FCSTD DOCUMENT  (FreeCAD 0.21R33694 (Git))
Label: charger
License: All rights reserved
LicenseURL: http://en.wikipedia.org/wiki/All_rights_reserved
objects: Part::Feature×111, App::Part×21, Sketcher::SketchObject×17, PartDesign::Pocket×9, PartDesign::Pad×8, PartDesign::Fillet×7, Part::FeaturePython×5, Part::Box×2, PartDesign::Body×2, App::DocumentObjectGroup×1
note: 185 computed .brp shape members not serialized (recipe doc carries the construction recipe); baked Part::Feature solids carry a one-line shape summary decoded from their .brp

FEATURE [Part::Box] Box002  label="Cube002"
  AttacherType = Attacher::AttachEngine3D
  Height = 13
  Length = 9
  Placement = pos=(3.5,14,-13) rot=(0,0,1;0rad)
  Width = 9
FEATURE [Part::Box] Box003  label="Cube003"
  AttacherType = Attacher::AttachEngine3D
  Height = 6
  Length = 10
  Placement = pos=(2.5,3,-6) rot=(0,0,1;0rad)
  Width = 6
FEATURE [Part::Feature] Part__Feature  label="v & a metr"
  shape: bbox 48 x 28.9 x 21.79 mm, 178 faces (baked)
FEATURE [App::Part] Part  label="VA indicator"
  Group = -> [Box002,Box003,Part__Feature]
  Origin = -> Origin
FEATURE [Part::Feature] Part__Feature001  label="Basetta"
  shape: bbox 51 x 26 x 1.7 mm, 150 faces (baked)
FEATURE [Part::Feature] Part__Feature002  label="DG301-5.0-02 v1"
  Placement = pos=(4,19.4,1.6) rot=(0,0,-1;1.5708rad)
  shape: bbox 7.6 x 10.6 x 10 mm, 75 faces (baked)
FEATURE [Part::Feature] Part__Feature003  label="DG301-5.0-02 v002"
  Placement = pos=(4,19.4,1.6) rot=(0,0,-1;1.5708rad)
  shape: bbox 4.003 x 4.003 x 9.803 mm, 11 faces (baked)
FEATURE [Part::Feature] Part__Feature004  label="DG301-5.0-02 v003"
  Placement = pos=(4,19.4,1.6) rot=(0,0,-1;1.5708rad)
  shape: bbox 5.55 x 3.9 x 2.851 mm, 29 faces (baked)
FEATURE [Part::Feature] Part__Feature005  label="DG301-5.0-02 v004"
  Placement = pos=(4,19.4,1.6) rot=(0,0,-1;1.5708rad)
  shape: bbox 3.898 x 3.8 x 5.801 mm, 14 faces (baked)
FEATURE [Part::Feature] Part__Feature006  label="DG301-5.0-02 v005"
  Placement = pos=(4,19.4,1.6) rot=(0,0,-1;1.5708rad)
  shape: bbox 4.003 x 4.003 x 9.803 mm, 11 faces (baked)
FEATURE [Part::Feature] Part__Feature007  label="DG301-5.0-02 v006"
  Placement = pos=(4,19.4,1.6) rot=(0,0,-1;1.5708rad)
  shape: bbox 5.55 x 3.9 x 2.851 mm, 29 faces (baked)
FEATURE [Part::Feature] Part__Feature008  label="DG301-5.0-02 v007"
  Placement = pos=(4,19.4,1.6) rot=(0,0,-1;1.5708rad)
  shape: bbox 3.898 x 3.8 x 5.801 mm, 14 faces (baked)
FEATURE [App::Part] DG301_5_0_02_v1  label="DG301-5.0-02 v008"
  Group = -> [Part__Feature002,Part__Feature003,Part__Feature004,Part__Feature005,Part__Feature006,Part__Feature007,Part__Feature008]
  Origin = -> Origin001
FEATURE [Part::Feature] Part__Feature009  label="DG301-5.0-02 v009"
  Placement = pos=(47,6.6,1.6) rot=(0,0,1;1.5708rad)
  shape: bbox 7.6 x 10.6 x 10 mm, 75 faces (baked)
FEATURE [Part::Feature] Part__Feature010  label="DG301-5.0-02 v010"
  Placement = pos=(47,6.6,1.6) rot=(0,0,1;1.5708rad)
  shape: bbox 4.003 x 4.003 x 9.803 mm, 11 faces (baked)
FEATURE [Part::Feature] Part__Feature011  label="DG301-5.0-02 v011"
  Placement = pos=(47,6.6,1.6) rot=(0,0,1;1.5708rad)
  shape: bbox 5.55 x 3.9 x 2.851 mm, 29 faces (baked)
FEATURE [Part::Feature] Part__Feature012  label="DG301-5.0-02 v012"
  Placement = pos=(47,6.6,1.6) rot=(0,0,1;1.5708rad)
  shape: bbox 3.898 x 3.8 x 5.801 mm, 14 faces (baked)
FEATURE [Part::Feature] Part__Feature013  label="DG301-5.0-02 v013"
  Placement = pos=(47,6.6,1.6) rot=(0,0,1;1.5708rad)
  shape: bbox 4.003 x 4.003 x 9.803 mm, 11 faces (baked)
FEATURE [Part::Feature] Part__Feature014  label="DG301-5.0-02 v014"
  Placement = pos=(47,6.6,1.6) rot=(0,0,1;1.5708rad)
  shape: bbox 5.55 x 3.9 x 2.851 mm, 29 faces (baked)
FEATURE [Part::Feature] Part__Feature015  label="DG301-5.0-02 v015"
  Placement = pos=(47,6.6,1.6) rot=(0,0,1;1.5708rad)
  shape: bbox 3.898 x 3.8 x 5.801 mm, 14 faces (baked)
FEATURE [App::Part] DG301_5_0_02_v002  label="DG301-5.0-02 v016"
  Group = -> [Part__Feature009,Part__Feature010,Part__Feature011,Part__Feature012,Part__Feature013,Part__Feature014,Part__Feature015]
  Origin = -> Origin002
FEATURE [Part::Feature] Part__Feature016  label="CAPACITOR 10x10 SMD v1"
  Placement = pos=(9.325,5.925,1.6) rot=(1,0,0;1.5708rad)
  shape: bbox 1 x 2 x 0.2 mm, 6 faces (baked)
FEATURE [Part::Feature] Part__Feature017  label="CAPACITOR 10x10 SMD v002"
  Placement = pos=(9.325,5.925,1.6) rot=(1,0,0;1.5708rad)
  shape: bbox 1 x 2 x 0.2 mm, 6 faces (baked)
FEATURE [Part::Feature] Part__Feature018  label="CAPACITOR 10x10 SMD v003"
  Placement = pos=(9.325,5.925,1.6) rot=(1,0,0;1.5708rad)
  shape: bbox 10.25 x 10.25 x 1.5 mm, 32 faces (baked)
FEATURE [Part::Feature] Part__Feature019  label="CAPACITOR 10x10 SMD v004"
  Placement = pos=(9.325,5.925,1.6) rot=(1,0,0;1.5708rad)
  shape: bbox 10.82 x 10.82 x 9.61 mm, 201 faces (baked)
FEATURE [App::Part] CAPACITOR_10x10_SMD_v1  label="CAPACITOR 10x10 SMD v005"
  Group = -> [Part__Feature016,Part__Feature017,Part__Feature018,Part__Feature019]
  Origin = -> Origin003
FEATURE [Part::Feature] Part__Feature020  label="CAPACITOR 10x10 SMD v006"
  Placement = pos=(41.475,19.975,1.6) rot=(0.57735,-0.57735,-0.57735;2.0944rad)
  shape: bbox 2 x 1 x 0.2 mm, 6 faces (baked)
FEATURE [Part::Feature] Part__Feature021  label="CAPACITOR 10x10 SMD v007"
  Placement = pos=(41.475,19.975,1.6) rot=(0.57735,-0.57735,-0.57735;2.0944rad)
  shape: bbox 2 x 1 x 0.2 mm, 6 faces (baked)
FEATURE [Part::Feature] Part__Feature022  label="CAPACITOR 10x10 SMD v008"
  Placement = pos=(41.475,19.975,1.6) rot=(0.57735,-0.57735,-0.57735;2.0944rad)
  shape: bbox 10.25 x 10.25 x 1.5 mm, 32 faces (baked)
FEATURE [Part::Feature] Part__Feature023  label="CAPACITOR 10x10 SMD v009"
  Placement = pos=(41.475,19.975,1.6) rot=(0.57735,-0.57735,-0.57735;2.0944rad)
  shape: bbox 10.82 x 10.82 x 9.61 mm, 201 faces (baked)
FEATURE [App::Part] CAPACITOR_10x10_SMD_v002  label="CAPACITOR 10x10 SMD v010"
  Group = -> [Part__Feature020,Part__Feature021,Part__Feature022,Part__Feature023]
  Origin = -> Origin004
FEATURE [Part::Feature] Part__Feature024  label="Trimpot 3296W v1"
  Placement = pos=(26.715,20.735,1.6) rot=(0,0,-1;1.5708rad)
  shape: bbox 4.83 x 9.53 x 14.15 mm, 96 faces (baked)
FEATURE [Part::Feature] Part__Feature025  label="Trimpot 3296W v002"
  Placement = pos=(32.265,20.735,1.6) rot=(0,0,-1;1.5708rad)
  shape: bbox 4.83 x 9.53 x 14.15 mm, 96 faces (baked)
FEATURE [Part::Feature] Part__Feature026  label="DO-214AB v1"
  Placement = pos=(18.1,1.725,1.6) rot=(0,0,1;1.5708rad)
  shape: bbox 3.2 x 1.6 x 1.55 mm, 14 faces (baked)
FEATURE [Part::Feature] Part__Feature027  label="DO-214AB v002"
  Placement = pos=(18.1,1.725,1.6) rot=(0,0,1;1.5708rad)
  shape: bbox 3.2 x 1.6 x 1.55 mm, 14 faces (baked)
FEATURE [Part::Feature] Part__Feature028  label="DO-214AB v003"
  Placement = pos=(18.1,1.725,1.6) rot=(0,0,1;1.5708rad)
  shape: bbox 6.25 x 7.15 x 2.51 mm, 142 faces (baked)
FEATURE [App::Part] DO_214AB_v1  label="DO-214AB v004"
  Group = -> [Part__Feature026,Part__Feature027,Part__Feature028]
  Origin = -> Origin005
FEATURE [Part::Feature] Part__Feature029  label="XL4015 TO263-5-1 v1"
  Placement = pos=(18.4666,17.0892,1.56535) rot=(0.003442,-0.003442,-0.999988;1.57081rad)
  shape: bbox 5.993 x 7.862 x 3.051 mm, 22 faces (baked)
FEATURE [Part::Feature] Part__Feature030  label="XL4015 TO263-5-1 v002"
  Placement = pos=(18.4666,17.0892,1.56535) rot=(0.003442,-0.003442,-0.999988;1.57081rad)
  shape: bbox 5.993 x 7.862 x 3.051 mm, 22 faces (baked)
FEATURE [Part::Feature] Part__Feature031  label="XL4015 TO263-5-1 v003"
  Placement = pos=(18.4666,17.0892,1.56535) rot=(0.003442,-0.003442,-0.999988;1.57081rad)
  shape: bbox 5.993 x 7.862 x 3.051 mm, 22 faces (baked)
FEATURE [Part::Feature] Part__Feature032  label="XL4015 TO263-5-1 v004"
  Placement = pos=(18.4666,17.0892,1.56535) rot=(0.003442,-0.003442,-0.999988;1.57081rad)
  shape: bbox 5.993 x 7.862 x 3.051 mm, 22 faces (baked)
FEATURE [Part::Feature] Part__Feature033  label="XL4015 TO263-5-1 v005"
  Placement = pos=(18.4666,17.0892,1.56535) rot=(0.003442,-0.003442,-0.999988;1.57081rad)
  shape: bbox 5.993 x 7.862 x 3.051 mm, 22 faces (baked)
FEATURE [Part::Feature] Part__Feature034  label="XL4015 TO263-5-1 v006"
  Placement = pos=(18.4666,17.0892,1.56535) rot=(0.003442,-0.003442,-0.999988;1.57081rad)
  shape: bbox 7.72 x 9.485 x 2.282 mm, 76 faces (baked)
FEATURE [Part::Feature] Part__Feature035  label="XL4015 TO263-5-1 v007"
  Placement = pos=(18.4666,17.0892,1.56535) rot=(0.003442,-0.003442,-0.999988;1.57081rad)
  shape: bbox 9.06 x 21.26 x 4.162 mm, 422 faces (baked)
FEATURE [App::Part] XL4015_TO263_5_1_v1  label="XL4015 TO263-5-1 v008"
  Group = -> [Part__Feature029,Part__Feature030,Part__Feature031,Part__Feature032,Part__Feature033,Part__Feature034,Part__Feature035]
  Origin = -> Origin006
FEATURE [Part::Feature] Part__Feature036  label="LM358 SOIC08 v1"
  Placement = pos=(37,6,1.55) rot=(0,0,-1;1.5708rad)
  shape: bbox 4 x 5 x 1.76 mm, 388 faces (baked)
FEATURE [Part::Feature] Part__Feature037  label="LM358 SOIC08 v002"
  Placement = pos=(37,6,1.55) rot=(0,0,-1;1.5708rad)
  shape: bbox 1.585 x 0.5401 x 1.25 mm, 38 faces (baked)
FEATURE [Part::Feature] Part__Feature038  label="LM358 SOIC08 v003"
  Placement = pos=(37,6,1.55) rot=(0,0,-1;1.5708rad)
  shape: bbox 1.585 x 0.5401 x 1.25 mm, 38 faces (baked)
FEATURE [Part::Feature] Part__Feature039  label="LM358 SOIC08 v004"
  Placement = pos=(37,6,1.55) rot=(0,0,-1;1.5708rad)
  shape: bbox 1.585 x 0.5401 x 1.25 mm, 38 faces (baked)
FEATURE [Part::Feature] Part__Feature040  label="LM358 SOIC08 v005"
  Placement = pos=(37,6,1.55) rot=(0,0,-1;1.5708rad)
  shape: bbox 1.585 x 0.5401 x 1.25 mm, 38 faces (baked)
FEATURE [Part::Feature] Part__Feature041  label="LM358 SOIC08 v006"
  Placement = pos=(37,6,1.55) rot=(0,0,-1;1.5708rad)
  shape: bbox 1.585 x 0.54 x 1.25 mm, 38 faces (baked)
FEATURE [Part::Feature] Part__Feature042  label="LM358 SOIC08 v007"
  Placement = pos=(37,6,1.55) rot=(0,0,-1;1.5708rad)
  shape: bbox 1.585 x 0.54 x 1.25 mm, 38 faces (baked)
FEATURE [Part::Feature] Part__Feature043  label="LM358 SOIC08 v008"
  Placement = pos=(37,6,1.55) rot=(0,0,-1;1.5708rad)
  shape: bbox 1.585 x 0.54 x 1.25 mm, 38 faces (baked)
FEATURE [Part::Feature] Part__Feature044  label="LM358 SOIC08 v009"
  Placement = pos=(37,6,1.55) rot=(0,0,-1;1.5708rad)
  shape: bbox 1.67 x 0.5557 x 1.266 mm, 72 faces (baked)
FEATURE [App::Part] LM358_SOIC08_v1  label="LM358 SOIC08 v010"
  Group = -> [Part__Feature036,Part__Feature037,Part__Feature038,Part__Feature039,Part__Feature040,Part__Feature041,Part__Feature042,Part__Feature043,Part__Feature044]
  Origin = -> Origin007
FEATURE [Part::Feature] Part__Feature045  label="Toro"
  Placement = pos=(0.4,28,-5) rot=(0,0,1;0rad)
  shape: bbox 13.49 x 12.99 x 6 mm, 13 faces (baked)
FEATURE [Part::Feature] Part__Feature046  label="Spira"
  Placement = pos=(0.4,28,-5) rot=(0,0,1;0.261799rad)
  shape: bbox 4.556 x 2.973 x 7.922 mm, 11 faces (baked)
FEATURE [Part::Feature] Part__Feature047  label="Spira001"
  Placement = pos=(0.4,28,-5) rot=(0,0,1;0.523599rad)
  shape: bbox 4.211 x 3.72 x 7.922 mm, 11 faces (baked)
FEATURE [Part::Feature] Part__Feature048  label="Spira002"
  Placement = pos=(0.4,28,-5) rot=(0,0,1;0.785398rad)
  shape: bbox 3.661 x 4.213 x 7.922 mm, 11 faces (baked)
FEATURE [Part::Feature] Part__Feature049  label="Spira003"
  Placement = pos=(0.4,28,-5) rot=(0,0,1;1.0472rad)
  shape: bbox 2.925 x 4.556 x 7.922 mm, 11 faces (baked)
FEATURE [Part::Feature] Part__Feature050  label="Spira004"
  Placement = pos=(0.4,28,-5) rot=(0,0,1;1.309rad)
  shape: bbox 2.396 x 4.592 x 7.922 mm, 11 faces (baked)
FEATURE [Part::Feature] Part__Feature051  label="Spira005"
  Placement = pos=(0.4,28,-5) rot=(0,0,1;1.5708rad)
  shape: bbox 2.396 x 4.592 x 7.922 mm, 11 faces (baked)
FEATURE [Part::Feature] Part__Feature052  label="Spira006"
  Placement = pos=(0.4,28,-5) rot=(0,0,1;1.8326rad)
  shape: bbox 2.973 x 4.556 x 7.922 mm, 11 faces (baked)
FEATURE [Part::Feature] Part__Feature053  label="Spira007"
  Placement = pos=(0.4,28,-5) rot=(0,0,1;2.0944rad)
  shape: bbox 3.72 x 4.211 x 7.922 mm, 11 faces (baked)
FEATURE [Part::Feature] Part__Feature054  label="Spira008"
  Placement = pos=(0.4,28,-5) rot=(0,0,1;2.35619rad)
  shape: bbox 4.213 x 3.661 x 7.922 mm, 11 faces (baked)
FEATURE [Part::Feature] Part__Feature055  label="Spira009"
  Placement = pos=(0.4,28,-5) rot=(0,0,1;2.61799rad)
  shape: bbox 4.556 x 2.925 x 7.922 mm, 11 faces (baked)
FEATURE [Part::Feature] Part__Feature056  label="Spira010"
  Placement = pos=(0.4,28,-5) rot=(0,0,1;2.87979rad)
  shape: bbox 4.592 x 2.396 x 7.922 mm, 11 faces (baked)
FEATURE [Part::Feature] Part__Feature057  label="Spira011"
  Placement = pos=(0.4,28,-5) rot=(0,0,1;3.14159rad)
  shape: bbox 4.592 x 2.396 x 7.922 mm, 11 faces (baked)
FEATURE [Part::Feature] Part__Feature058  label="Spira012"
  Placement = pos=(0.4,28,-5) rot=(0,0,1;3.40339rad)
  shape: bbox 4.556 x 2.973 x 7.922 mm, 11 faces (baked)
FEATURE [Part::Feature] Part__Feature059  label="Spira013"
  Placement = pos=(0.4,28,-5) rot=(0,0,1;3.66519rad)
  shape: bbox 4.211 x 3.72 x 7.922 mm, 11 faces (baked)
FEATURE [Part::Feature] Part__Feature060  label="Spira014"
  Placement = pos=(0.4,28,-5) rot=(0,0,1;3.92699rad)
  shape: bbox 3.661 x 4.213 x 7.922 mm, 11 faces (baked)
FEATURE [Part::Feature] Part__Feature061  label="Spira015"
  Placement = pos=(0.4,28,-5) rot=(0,0,1;4.18879rad)
  shape: bbox 2.925 x 4.556 x 7.922 mm, 11 faces (baked)
FEATURE [Part::Feature] Part__Feature062  label="Spira016"
  Placement = pos=(0.4,28,-5) rot=(0,0,-1;1.8326rad)
  shape: bbox 2.396 x 4.592 x 7.922 mm, 11 faces (baked)
FEATURE [Part::Feature] Part__Feature063  label="Spira017"
  Placement = pos=(0.4,28,-5) rot=(0,0,-1;1.5708rad)
  shape: bbox 2.396 x 4.592 x 7.922 mm, 11 faces (baked)
FEATURE [Part::Feature] Part__Feature064  label="Spira018"
  Placement = pos=(0.4,28,-5) rot=(0,0,-1;1.309rad)
  shape: bbox 2.973 x 4.556 x 7.922 mm, 11 faces (baked)
FEATURE [Part::Feature] Part__Feature065  label="Spira019"
  Placement = pos=(0.4,28,-5) rot=(0,0,-1;1.0472rad)
  shape: bbox 3.72 x 4.211 x 7.922 mm, 11 faces (baked)
FEATURE [Part::Feature] Part__Feature066  label="Spira020"
  Placement = pos=(0.4,28,-5) rot=(0,0,-1;0.785398rad)
  shape: bbox 4.213 x 3.661 x 7.922 mm, 11 faces (baked)
FEATURE [Part::Feature] Part__Feature067  label="Spira021"
  Placement = pos=(0.4,28,-5) rot=(0,0,-1;0.523599rad)
  shape: bbox 4.556 x 2.925 x 7.922 mm, 11 faces (baked)
FEATURE [Part::Feature] Part__Feature068  label="SpiraCodA"
  Placement = pos=(0.401472,27.9945,-5) rot=(0,0,1;0.000874rad)
  shape: bbox 7.632 x 2.388 x 7.922 mm, 10 faces (baked)
FEATURE [Part::Feature] Part__Feature069  label="SpiraCpdB"
  Placement = pos=(0.399001,27.9963,-5) rot=(0,0,-1;0.261205rad)
  shape: bbox 7.645 x 2.398 x 7.933 mm, 10 faces (baked)
FEATURE [App::Part] Coil_v9  label="Coil v9"
  Group = -> [Part__Feature045,Part__Feature046,Part__Feature047,Part__Feature048,Part__Feature049,Part__Feature050,Part__Feature051,Part__Feature052,Part__Feature053,Part__Feature054,Part__Feature055,Part__Feature056,Part__Feature057,Part__Feature058,Part__Feature059,Part__Feature060,Part__Feature061,Part__Feature062,Part__Feature063,Part__Feature064,Part__Feature065,Part__Feature066,Part__Feature067,+2 more]
  Origin = -> Origin008
  Placement = pos=(2e-15,0,9) rot=(-0.57735,-0.57735,0.57735;4.18879rad)
FEATURE [Part::Feature] Part__Feature070  label="SOT-89 v1"
  Placement = pos=(31.81,12.82,1.6) rot=(0,0,1;1.5708rad)
  shape: bbox 1.429 x 0.42 x 0.41 mm, 20 faces (baked)
FEATURE [Part::Feature] Part__Feature071  label="SOT-89 v002"
  Placement = pos=(31.81,12.82,1.6) rot=(0,0,1;1.5708rad)
  shape: bbox 4 x 1.6 x 0.41 mm, 38 faces (baked)
FEATURE [Part::Feature] Part__Feature072  label="SOT-89 v003"
  Placement = pos=(31.81,12.82,1.6) rot=(0,0,1;1.5708rad)
  shape: bbox 1.429 x 0.42 x 0.41 mm, 20 faces (baked)
FEATURE [Part::Feature] Part__Feature073  label="SOT-89 v004"
  Placement = pos=(31.81,12.82,1.6) rot=(0,0,1;1.5708rad)
  shape: bbox 2.43 x 4.43 x 1.51 mm, 162 faces (baked)
FEATURE [App::Part] SOT_89_v1  label="SOT-89 v005"
  Group = -> [Part__Feature070,Part__Feature071,Part__Feature072,Part__Feature073]
  Origin = -> Origin009
FEATURE [Part::Feature] Part__Feature074  label="SC-59A v1"
  Placement = pos=(36.8,13.75,1.6) rot=(0,0,-1;1.5708rad)
  shape: bbox 1.75 x 3.1 x 1.35 mm, 34 faces (baked)
FEATURE [Part::Feature] Part__Feature075  label="SC-59A v002"
  Placement = pos=(36.8,13.75,1.6) rot=(0,0,-1;1.5708rad)
  shape: bbox 0.875 x 0.4 x 1 mm, 14 faces (baked)
FEATURE [Part::Feature] Part__Feature076  label="SC-59A v003"
  Placement = pos=(36.8,13.75,1.6) rot=(0,0,-1;1.5708rad)
  shape: bbox 0.875 x 0.4 x 1 mm, 14 faces (baked)
FEATURE [Part::Feature] Part__Feature077  label="SC-59A v004"
  Placement = pos=(36.8,13.75,1.6) rot=(0,0,-1;1.5708rad)
  shape: bbox 0.875 x 0.4 x 1 mm, 14 faces (baked)
FEATURE [App::Part] SC_59A_v1  label="SC-59A v005"
  Group = -> [Part__Feature074,Part__Feature075,Part__Feature076,Part__Feature077]
  Origin = -> Origin010
FEATURE [Part::Feature] Part__Feature078  label="LED v1"
  Placement = pos=(44.84,1.625,1.62) rot=(0.57735,-0.57735,-0.57735;2.0944rad)
  shape: bbox 0.95 x 1.15 x 0.1 mm, 8 faces (baked)
FEATURE [Part::Feature] Part__Feature079  label="LED v002"
  Placement = pos=(44.84,1.625,1.62) rot=(0.57735,-0.57735,-0.57735;2.0944rad)
  shape: bbox 1.34 x 1.258 x 0.6541 mm, 28 faces (baked)
FEATURE [Part::Feature] Part__Feature080  label="LED v003"
  Placement = pos=(44.84,1.625,1.62) rot=(0.57735,-0.57735,-0.57735;2.0944rad)
  shape: bbox 0.9304 x 1.15 x 0.1 mm, 14 faces (baked)
FEATURE [Part::Feature] Part__Feature081  label="LED v004"
  Placement = pos=(44.84,1.625,1.62) rot=(0.57735,-0.57735,-0.57735;2.0944rad)
  shape: bbox 0.3549 x 1.28 x 0.15 mm, 19 faces (baked)
FEATURE [Part::Feature] Part__Feature082  label="LED v005"
  Placement = pos=(44.84,1.625,1.62) rot=(0.57735,-0.57735,-0.57735;2.0944rad)
  shape: bbox 0.3549 x 1.28 x 0.15 mm, 19 faces (baked)
FEATURE [App::Part] LED_v1  label="LED v006"
  Group = -> [Part__Feature078,Part__Feature079,Part__Feature080,Part__Feature081,Part__Feature082]
  Origin = -> Origin011
FEATURE [Part::Feature] Part__Feature083  label="LED v007"
  Placement = pos=(39.84,1.625,1.62) rot=(0.57735,-0.57735,-0.57735;2.0944rad)
  shape: bbox 0.95 x 1.15 x 0.1 mm, 8 faces (baked)
FEATURE [Part::Feature] Part__Feature084  label="LED v008"
  Placement = pos=(39.84,1.625,1.62) rot=(0.57735,-0.57735,-0.57735;2.0944rad)
  shape: bbox 1.34 x 1.258 x 0.6541 mm, 28 faces (baked)
FEATURE [Part::Feature] Part__Feature085  label="LED v009"
  Placement = pos=(39.84,1.625,1.62) rot=(0.57735,-0.57735,-0.57735;2.0944rad)
  shape: bbox 0.9304 x 1.15 x 0.1 mm, 14 faces (baked)
FEATURE [Part::Feature] Part__Feature086  label="LED v010"
  Placement = pos=(39.84,1.625,1.62) rot=(0.57735,-0.57735,-0.57735;2.0944rad)
  shape: bbox 0.3549 x 1.28 x 0.15 mm, 19 faces (baked)
FEATURE [Part::Feature] Part__Feature087  label="LED v011"
  Placement = pos=(39.84,1.625,1.62) rot=(0.57735,-0.57735,-0.57735;2.0944rad)
  shape: bbox 0.3549 x 1.28 x 0.15 mm, 19 faces (baked)
FEATURE [App::Part] LED_v002  label="LED v012"
  Group = -> [Part__Feature083,Part__Feature084,Part__Feature085,Part__Feature086,Part__Feature087]
  Origin = -> Origin012
FEATURE [Part::Feature] Part__Feature088  label="LED v013"
  Placement = pos=(20.16,23.875,1.62) rot=(0.57735,-0.57735,-0.57735;2.0944rad)
  shape: bbox 0.95 x 1.15 x 0.1 mm, 8 faces (baked)
FEATURE [Part::Feature] Part__Feature089  label="LED v014"
  Placement = pos=(20.16,23.875,1.62) rot=(0.57735,-0.57735,-0.57735;2.0944rad)
  shape: bbox 1.34 x 1.258 x 0.6541 mm, 28 faces (baked)
FEATURE [Part::Feature] Part__Feature090  label="LED v015"
  Placement = pos=(20.16,23.875,1.62) rot=(0.57735,-0.57735,-0.57735;2.0944rad)
  shape: bbox 0.9304 x 1.15 x 0.1 mm, 14 faces (baked)
FEATURE [Part::Feature] Part__Feature091  label="LED v016"
  Placement = pos=(20.16,23.875,1.62) rot=(0.57735,-0.57735,-0.57735;2.0944rad)
  shape: bbox 0.3549 x 1.28 x 0.15 mm, 19 faces (baked)
FEATURE [Part::Feature] Part__Feature092  label="LED v017"
  Placement = pos=(20.16,23.875,1.62) rot=(0.57735,-0.57735,-0.57735;2.0944rad)
  shape: bbox 0.3549 x 1.28 x 0.15 mm, 19 faces (baked)
FEATURE [App::Part] LED_v003  label="LED v018"
  Group = -> [Part__Feature088,Part__Feature089,Part__Feature090,Part__Feature091,Part__Feature092]
  Origin = -> Origin013
FEATURE [App::Part] XL4015_StepDown_DC_DC_5A__CC_CV__v1  label="XL4015 StepDown DC-DC 5A (CC-CV) v1"
  Group = -> [Part__Feature001,DG301_5_0_02_v1,DG301_5_0_02_v002,CAPACITOR_10x10_SMD_v1,CAPACITOR_10x10_SMD_v002,Part__Feature024,Part__Feature025,DO_214AB_v1,XL4015_TO263_5_1_v1,LM358_SOIC08_v1,Coil_v9,SOT_89_v1,SC_59A_v1,LED_v1,LED_v002,LED_v003]
  Origin = -> Origin014
  Placement = pos=(45,-6,10) rot=(0,-0.707107,0.707107;3.14159rad)
FEATURE [Part::Feature] Part__Feature093  label="Vypinac kolebkovy_KCD1-11_2pin"
  shape: bbox 15.5 x 10.5 x 10.8 mm, 3982 faces (baked)
FEATURE [Part::Feature] Part__Feature094  label="Vypinac kolebkovy_KCD1-11_2pin001"
  shape: bbox 10.61 x 7.809 x 8.803 mm, 80 faces (baked)
FEATURE [Part::Feature] Part__Feature095  label="Vypinac kolebkovy_KCD1-11_2pin002"
  shape: bbox 3 x 6 x 9.4 mm, 67 faces (baked)
FEATURE [Part::Feature] Part__Feature096  label="Vypinac kolebkovy_KCD1-11_2pin003"
  shape: bbox 1.002 x 6.002 x 10.8 mm, 77 faces (baked)
FEATURE [Part::Feature] Part__Feature097  label="Vypinac kolebkovy_KCD1-11_2pin004"
  shape: bbox 8.5 x 5 x 3.939 mm, 68 faces (baked)
FEATURE [Part::Feature] Part__Feature098  label="Vypinac kolebkovy_KCD1-11_2pin005"
  shape: bbox 3.601 x 2.4 x 6.147 mm, 9 faces (baked)
FEATURE [Part::Feature] Part__Feature099  label="Vypinac kolebkovy_KCD1-11_2pin006"
  shape: bbox 3.969 x 2.945 x 7.276 mm, 54 faces (baked)
FEATURE [Part::Feature] Part__Feature100  label="Vypinac kolebkovy_KCD1-11_2pin007"
  shape: bbox 2.462 x 2.437 x 0.2543 mm, 6 faces (baked)
FEATURE [Part::Feature] Part__Feature101  label="Vypinac kolebkovy_KCD1-11_2pin008"
  shape: bbox 2.189 x 0.5 x 1.014 mm, 6 faces (baked)
FEATURE [App::Part] Vypinac_kolebkovy_KCD1_11_2pin  label="Vypinac kolebkovy_KCD1-11_2pin009"
  Group = -> [Part__Feature093,Part__Feature094,Part__Feature095,Part__Feature096,Part__Feature097,Part__Feature098,Part__Feature099,Part__Feature100,Part__Feature101]
  Origin = -> Origin016
  Placement = pos=(-10,8,15) rot=(0,0,1;-1.5708rad)
FEATURE [App::Part] Part001  label="инд+заряд-л-в"
  Group = -> [Part,XL4015_StepDown_DC_DC_5A__CC_CV__v1,Vypinac_kolebkovy_KCD1_11_2pin]
  Origin = -> Origin015
FEATURE [Part::FeaturePython] Clone  label="инд+заряд-л-н"  # Draft clone (typed FeaturePython)
  AttacherType = Attacher::AttachEngine3D
  Fuse = false
  Objects = -> [Part001]
  Placement = pos=(0,-50,0) rot=(0,0,1;0rad)
  Scale = (1,1,1)
FEATURE [Part::FeaturePython] Clone001  label="VA indicator001"  # Draft clone (typed FeaturePython)
  AttacherType = Attacher::AttachEngine3D
  Fuse = false
  Objects = -> [Part]
  Scale = (1,1,1)
FEATURE [Part::FeaturePython] Clone002  label="XL4015 StepDown DC-DC 5A (CC-CV) v002"  # Draft clone (typed FeaturePython)
  AttacherType = Attacher::AttachEngine3D
  Fuse = false
  Objects = -> [XL4015_StepDown_DC_DC_5A__CC_CV__v1]
  Placement = pos=(0,-6,-16) rot=(1,0,0;1.5708rad)
  Scale = (1,1,1)
FEATURE [Part::FeaturePython] Clone003  label="Vypinac kolebkovy_KCD1-11_2pin010"  # Draft clone (typed FeaturePython)
  AttacherType = Attacher::AttachEngine3D
  Fuse = false
  Objects = -> [Vypinac_kolebkovy_KCD1_11_2pin]
  Placement = pos=(55,8,15) rot=(0,0,-1;1.5708rad)
  Scale = (1,1,1)
FEATURE [App::Part] Part002  label="инд+заряд-п-в"
  Group = -> [Clone001,Clone002,Clone003]
  Origin = -> Origin017
  Placement = pos=(55,0,0) rot=(0,0,1;0rad)
FEATURE [Part::FeaturePython] Clone004  label="инд+заряд-п-н"  # Draft clone (typed FeaturePython)
  AttacherType = Attacher::AttachEngine3D
  Fuse = false
  Objects = -> [Part002]
  Placement = pos=(55,-50,0) rot=(0,0,1;0rad)
  Scale = (1,1,1)
FEATURE [Part::Feature] Part__Feature102  label="COMPOUND"
  shape: bbox 2.5 x 4.9 x 0.25 mm, 8 faces (baked)
FEATURE [Part::Feature] Part__Feature103  label="COMPOUND001"
  shape: bbox 2 x 2 x 0.6 mm, 4 faces (baked)
FEATURE [Part::Feature] Part__Feature104  label="COMPOUND002"
  shape: bbox 0.4 x 9 x 2 mm, 8 faces (baked)
FEATURE [Part::Feature] Part__Feature105  label="COMPOUND003"
  shape: bbox 9.001 x 13.8 x 12 mm, 31 faces (baked)
FEATURE [Part::Feature] Part__Feature106  label="COMPOUND004"
  shape: bbox 1.93 x 1.93 x 7.874 mm, 6 faces (baked)
FEATURE [Part::Feature] Part__Feature107  label="COMPOUND005"
  shape: bbox 4.5 x 13.55 x 0.3 mm, 12 faces (baked)
FEATURE [Part::Feature] Part__Feature108  label="COMPOUND006"
  shape: bbox 5.194 x 1.117 x 4.664 mm, 10 faces (baked)
FEATURE [Part::Feature] Part__Feature109  label="COMPOUND007"
  shape: bbox 7.2 x 10.5 x 6.575 mm, 22 faces (baked)
FEATURE [App::Part] COMPOUND  label="COMPOUND008"
  Group = -> [Part__Feature102,Part__Feature103,Part__Feature104,Part__Feature105,Part__Feature106,Part__Feature107,Part__Feature108,Part__Feature109]
  Origin = -> Origin018
FEATURE [App::Part] DC_005  label="DC-005"
  Group = -> [COMPOUND]
  Origin = -> Origin019
  Placement = pos=(-1.968,-0.026,1.65) rot=(0.57735,-0.57735,-0.57735;2.0944rad)
FEATURE [Part::Feature] Part__Feature110  label="dc PCB"
  shape: bbox 13.97 x 29.21 x 1.6 mm, 74 faces (baked)
FEATURE [App::Part] dc_1  label="dc 1"
  Group = -> [DC_005,Part__Feature110]
  Origin = -> Origin020
  Placement = pos=(50,-68,-18) rot=(0,0,1;1.5708rad)
FEATURE [App::DocumentObjectGroup] Group  label="элементы"
  Group = -> [Part001,Clone,Part002,Clone004,dc_1]
FEATURE [Sketcher::SketchObject] Sketch
  FullyConstrained = true
  MapMode = 5
  Support = -> [XY_Plane021]
  sketch-geometry (4):
    g0: LineSegment StartX=-20 StartY=33 StartZ=0 EndX=120 EndY=33 EndZ=0
    g1: LineSegment StartX=120 StartY=33 StartZ=0 EndX=120 EndY=-77 EndZ=0
    g2: LineSegment StartX=120 StartY=-77 StartZ=0 EndX=-20 EndY=-77 EndZ=0
    g3: LineSegment StartX=-20 StartY=-77 StartZ=0 EndX=-20 EndY=33 EndZ=0
  constraints (12):
    c: Coincident(g0,g1)
    c: Coincident(g1,g2)
    c: Coincident(g2,g3)
    c: Coincident(g3,g0)
    c: Horizontal(g0)
    c: Horizontal(g2)
    c: Vertical(g1)
    c: Vertical(g3)
    c: DistanceX(g0,g0) = 140
    c: DistanceY(g3,g3) = 110
    c: DistanceX(g0,g-1) = 20
    c: DistanceY(g-1,g0) = 33
FEATURE [PartDesign::Pad] Pad  label="коробка"
  Direction = (0,0,1)
  Length = 18
  Length2 = 10
  Profile = -> Sketch
  ReferenceAxis = -> Sketch [N_Axis]
  Reversed = true
  Type = 0
FEATURE [Sketcher::SketchObject] Sketch001
  FullyConstrained = true
  MapMode = 5
  Placement = pos=(0,0,-18) rot=(1,0,0;3.14159rad)
  Support = -> [Pad]
  sketch-geometry (4):
    g0: LineSegment StartX=-18 StartY=75 StartZ=0 EndX=118 EndY=75 EndZ=0
    g1: LineSegment StartX=118 StartY=75 StartZ=0 EndX=118 EndY=-31 EndZ=0
    g2: LineSegment StartX=118 StartY=-31 StartZ=0 EndX=-18 EndY=-31 EndZ=0
    g3: LineSegment StartX=-18 StartY=-31 StartZ=0 EndX=-18 EndY=75 EndZ=0
  constraints (12):
    c: Coincident(g0,g1)
    c: Coincident(g1,g2)
    c: Coincident(g2,g3)
    c: Coincident(g3,g0)
    c: Horizontal(g0)
    c: Horizontal(g2)
    c: Vertical(g1)
    c: Vertical(g3)
    c: DistanceX(g0,g0) = 136
    c: DistanceY(g3,g3) = 106
    c: DistanceX(g2,g-1) = 18
    c: DistanceY(g2,g-1) = 31
FEATURE [PartDesign::Pocket] Pocket  label="глубина"
  BaseFeature = -> Pad
  Direction = (0,0,1)
  Length = 16
  Length2 = 5
  Profile = -> Sketch001
  ReferenceAxis = -> Sketch001 [N_Axis]
  Type = 0
FEATURE [Sketcher::SketchObject] Sketch002
  ExternalGeometry = -> [Pocket]
  FullyConstrained = true
  MapMode = 5
  Placement = pos=(0,0,-2) rot=(1,0,0;3.14159rad)
  Support = -> [Pocket]
  sketch-geometry (24):
    g0: LineSegment StartX=-18 StartY=75 StartZ=0 EndX=-18 EndY=67 EndZ=0
    g1: LineSegment StartX=-18 StartY=75 StartZ=0 EndX=-10 EndY=75 EndZ=0
    g2: ArcOfCircle CenterX=-14 CenterY=71 CenterZ=0 NormalX=0 NormalY=0 NormalZ=1 AngleXU=0 Radius=4 StartAngle=4.71239 EndAngle=6.28319
    g3: LineSegment StartX=-18 StartY=67 StartZ=0 EndX=-14 EndY=67 EndZ=0
    g4: LineSegment StartX=-10 StartY=75 StartZ=0 EndX=-10 EndY=71 EndZ=0
    g5: Circle CenterX=-14 CenterY=71 CenterZ=0 NormalX=0 NormalY=0 NormalZ=1 AngleXU=0 Radius=1.1
    g6: LineSegment StartX=-18 StartY=-31 StartZ=0 EndX=-10 EndY=-31 EndZ=0
    g7: LineSegment StartX=-18 StartY=-31 StartZ=0 EndX=-18 EndY=-23 EndZ=0
    g8: LineSegment StartX=-18 StartY=-23 StartZ=0 EndX=-14 EndY=-23 EndZ=0
    g9: LineSegment StartX=-10 StartY=-31 StartZ=0 EndX=-10 EndY=-27 EndZ=0
    g10: ArcOfCircle CenterX=-14 CenterY=-27 CenterZ=0 NormalX=0 NormalY=0 NormalZ=1 AngleXU=0 Radius=4 StartAngle=0 EndAngle=1.5708
    g11: Circle CenterX=-14 CenterY=-27 CenterZ=0 NormalX=0 NormalY=0 NormalZ=1 AngleXU=0 Radius=1.1
    g12: LineSegment StartX=118 StartY=75 StartZ=0 EndX=110 EndY=75 EndZ=0
    g13: LineSegment StartX=118 StartY=75 StartZ=0 EndX=118 EndY=67 EndZ=0
    g14: LineSegment StartX=110 StartY=75 StartZ=0 EndX=110 EndY=71 EndZ=0
    g15: LineSegment StartX=118 StartY=67 StartZ=0 EndX=114 EndY=67 EndZ=0
    g16: LineSegment StartX=118 StartY=-31 StartZ=0 EndX=110 EndY=-31 EndZ=0
    g17: LineSegment StartX=118 StartY=-31 StartZ=0 EndX=118 EndY=-23 EndZ=0
    g18: LineSegment StartX=110 StartY=-31 StartZ=0 EndX=110 EndY=-27 EndZ=0
    g19: LineSegment StartX=118 StartY=-23 StartZ=0 EndX=114 EndY=-23 EndZ=0
    g20: ArcOfCircle CenterX=114 CenterY=-27 CenterZ=0 NormalX=0 NormalY=0 NormalZ=1 AngleXU=0 Radius=4 StartAngle=1.5708 EndAngle=3.14159
    g21: ArcOfCircle CenterX=114 CenterY=71 CenterZ=0 NormalX=0 NormalY=0 NormalZ=1 AngleXU=0 Radius=4 StartAngle=3.14159 EndAngle=4.71239
    g22: Circle CenterX=114 CenterY=71 CenterZ=0 NormalX=0 NormalY=0 NormalZ=1 AngleXU=0 Radius=1.1
    g23: Circle CenterX=114 CenterY=-27 CenterZ=0 NormalX=0 NormalY=0 NormalZ=1 AngleXU=0 Radius=1.1
  constraints (68):
    c: Coincident(g0,g-3)
    c: Vertical(g0)
    c: Coincident(g1,g0)
    c: Horizontal(g1)
    c: Coincident(g3,g0)
    c: Horizontal(g3)
    c: Coincident(g4,g1)
    c: Vertical(g4)
    c: Coincident(g4,g2)
    c: Coincident(g3,g2)
    c: Vertical(g2,g2)
    c: Horizontal(g2,g2)
    c: Radius(g2) = 4
    c: Equal(g3,g4)
    c: DistanceX(g3,g3) = 4
    c: Coincident(g5,g2)
    c: Diameter(g5) = 2.2
    c: Coincident(g6,g-4)
    c: Horizontal(g6)
    c: Coincident(g7,g6)
    c: Vertical(g7)
    c: Coincident(g8,g7)
    c: Horizontal(g8)
    c: Coincident(g9,g6)
    c: Vertical(g9)
    c: Coincident(g10,g8)
    c: Coincident(g10,g9)
    c: Vertical(g10,g8)
    c: Vertical(g8,g2)
    c: Horizontal(g10,g9)
    c: Equal(g8,g9)
    c: Equal(g10,g2)
    c: Coincident(g11,g10)
    c: Equal(g5,g11)
    c: Coincident(g12,g-6)
    c: Horizontal(g12)
    c: Coincident(g13,g12)
    c: Vertical(g13)
    c: Coincident(g14,g12)
    c: Vertical(g14)
    c: Coincident(g15,g13)
    c: Horizontal(g15)
    c: Coincident(g16,g-5)
    c: Horizontal(g16)
    c: Coincident(g17,g16)
    c: Vertical(g17)
    c: Coincident(g18,g16)
    c: Vertical(g18)
    c: Coincident(g19,g17)
    c: Horizontal(g19)
    c: Coincident(g20,g18)
    c: Coincident(g20,g19)
    c: Coincident(g21,g15)
    c: Coincident(g21,g14)
    c: Vertical(g21,g15)
    c: Vertical(g15,g19)
    c: Vertical(g19,g20)
    c: Horizontal(g18,g20)
    c: Horizontal(g21,g14)
    c: Horizontal(g14,g2)
    c: Equal(g14,g15)
    c: Equal(g21,g2)
    c: Equal(g2,g20)
    c: Equal(g18,g19)
    c: Coincident(g22,g21)
    c: Coincident(g23,g20)
    c: Equal(g23,g22)
    c: Equal(g22,g5)
FEATURE [PartDesign::Pad] Pad001  label="стойки винтов"
  BaseFeature = -> Pocket
  Direction = (0,0,-1)
  Length = 20
  Length2 = 10
  Profile = -> Sketch002
  ReferenceAxis = -> Sketch002 [N_Axis]
  Type = 0
FEATURE [Sketcher::SketchObject] Sketch003
  FullyConstrained = true
  MapMode = 5
  Support = -> [Pad001]
  sketch-geometry (32):
    g0: LineSegment StartX=-0.4 StartY=26.2 StartZ=0 EndX=45.4 EndY=26.2 EndZ=0
    g1: LineSegment StartX=45.4 StartY=26.2 StartZ=0 EndX=45.4 EndY=-0.7 EndZ=0
    g2: LineSegment StartX=45.4 StartY=-0.7 StartZ=0 EndX=-0.4 EndY=-0.7 EndZ=0
    g3: LineSegment StartX=-0.4 StartY=-0.7 StartZ=0 EndX=-0.4 EndY=26.2 EndZ=0
    g4: LineSegment StartX=54.6 StartY=26.2 StartZ=0 EndX=100.4 EndY=26.2 EndZ=0
    g5: LineSegment StartX=100.4 StartY=26.2 StartZ=0 EndX=100.4 EndY=-0.7 EndZ=0
    g6: LineSegment StartX=100.4 StartY=-0.7 StartZ=0 EndX=54.6 EndY=-0.7 EndZ=0
    g7: LineSegment StartX=54.6 StartY=-0.7 StartZ=0 EndX=54.6 EndY=26.2 EndZ=0
    g8: LineSegment StartX=-0.4 StartY=-23.8 StartZ=0 EndX=45.4 EndY=-23.8 EndZ=0
    g9: LineSegment StartX=45.4 StartY=-23.8 StartZ=0 EndX=45.4 EndY=-50.7 EndZ=0
    g10: LineSegment StartX=45.4 StartY=-50.7 StartZ=0 EndX=-0.4 EndY=-50.7 EndZ=0
    g11: LineSegment StartX=-0.4 StartY=-50.7 StartZ=0 EndX=-0.4 EndY=-23.8 EndZ=0
    g12: LineSegment StartX=54.6 StartY=-23.8 StartZ=0 EndX=100.4 EndY=-23.8 EndZ=0
    g13: LineSegment StartX=100.4 StartY=-23.8 StartZ=0 EndX=100.4 EndY=-50.7 EndZ=0
    g14: LineSegment StartX=100.4 StartY=-50.7 StartZ=0 EndX=54.6 EndY=-50.7 EndZ=0
    g15: LineSegment StartX=54.6 StartY=-50.7 StartZ=0 EndX=54.6 EndY=-23.8 EndZ=0
    g16: LineSegment StartX=-14.65 StartY=15.15 StartZ=0 EndX=-5.35 EndY=15.15 EndZ=0
    g17: LineSegment StartX=-5.35 StartY=15.15 StartZ=0 EndX=-5.35 EndY=0.85 EndZ=0
    g18: LineSegment StartX=-5.35 StartY=0.85 StartZ=0 EndX=-14.65 EndY=0.85 EndZ=0
    g19: LineSegment StartX=-14.65 StartY=0.85 StartZ=0 EndX=-14.65 EndY=15.15 EndZ=0
    g20: LineSegment StartX=105.35 StartY=15.15 StartZ=0 EndX=114.65 EndY=15.15 EndZ=0
    g21: LineSegment StartX=114.65 StartY=15.15 StartZ=0 EndX=114.65 EndY=0.85 EndZ=0
    g22: LineSegment StartX=114.65 StartY=0.85 StartZ=0 EndX=105.35 EndY=0.85 EndZ=0
    g23: LineSegment StartX=105.35 StartY=0.85 StartZ=0 EndX=105.35 EndY=15.15 EndZ=0
    g24: LineSegment StartX=-14.65 StartY=-34.85 StartZ=0 EndX=-5.35 EndY=-34.85 EndZ=0
    g25: LineSegment StartX=-5.35 StartY=-34.85 StartZ=0 EndX=-5.35 EndY=-49.15 EndZ=0
    g26: LineSegment StartX=-5.35 StartY=-49.15 StartZ=0 EndX=-14.65 EndY=-49.15 EndZ=0
    g27: LineSegment StartX=-14.65 StartY=-49.15 StartZ=0 EndX=-14.65 EndY=-34.85 EndZ=0
    g28: LineSegment StartX=105.35 StartY=-34.85 StartZ=0 EndX=114.65 EndY=-34.85 EndZ=0
    g29: LineSegment StartX=114.65 StartY=-34.85 StartZ=0 EndX=114.65 EndY=-49.15 EndZ=0
    g30: LineSegment StartX=114.65 StartY=-49.15 StartZ=0 EndX=105.35 EndY=-49.15 EndZ=0
    g31: LineSegment StartX=105.35 StartY=-49.15 StartZ=0 EndX=105.35 EndY=-34.85 EndZ=0
  constraints (96):
    c: Coincident(g0,g1)
    c: Coincident(g1,g2)
    c: Coincident(g2,g3)
    c: Coincident(g3,g0)
    c: Horizontal(g0)
    c: Horizontal(g2)
    c: Vertical(g1)
    c: Vertical(g3)
    c: DistanceX(g0,g0) = 45.8
    c: DistanceY(g3,g3) = 26.9
    c: DistanceX(g2,g-1) = 0.4
    c: DistanceY(g2,g-1) = 0.7
    c: Coincident(g4,g5)
    c: Coincident(g5,g6)
    c: Coincident(g6,g7)
    c: Coincident(g7,g4)
    c: Horizontal(g4)
    c: Horizontal(g6)
    c: Vertical(g5)
    c: Vertical(g7)
    c: Coincident(g8,g9)
    c: Coincident(g9,g10)
    c: Coincident(g10,g11)
    c: Coincident(g11,g8)
    c: Horizontal(g8)
    c: Horizontal(g10)
    c: Vertical(g9)
    c: Vertical(g11)
    c: Coincident(g12,g13)
    c: Coincident(g13,g14)
    c: Coincident(g14,g15)
    c: Coincident(g15,g12)
    c: Horizontal(g12)
    c: Horizontal(g14)
    c: Vertical(g13)
    c: Vertical(g15)
    c: Horizontal(g0,g4)
    c: Equal(g3,g7)
    c: Equal(g3,g11)
    c: Equal(g3,g15)
    c: Equal(g0,g4)
    c: Equal(g0,g8)
    c: Equal(g0,g12)
    c: Vertical(g0,g8)
    c: Vertical(g4,g12)
    c: Horizontal(g8,g12)
    c: DistanceX(g0,g4) = 55
    c: DistanceY(g8,g0) = 50
    c: Coincident(g16,g17)
    c: Coincident(g17,g18)
    c: Coincident(g18,g19)
    c: Coincident(g19,g16)
    c: Horizontal(g16)
    c: Horizontal(g18)
    c: Vertical(g17)
    c: Vertical(g19)
    c: DistanceY(g17,g17) = 14.3
    c: DistanceX(g16,g16) = 9.3
    c: DistanceX(g17,g-1) = 5.35
    c: DistanceY(g-1,g17) = 0.85
    c: Coincident(g20,g21)
    c: Coincident(g21,g22)
    c: Coincident(g22,g23)
    c: Coincident(g23,g20)
    c: Horizontal(g20)
    c: Horizontal(g22)
    c: Vertical(g21)
    c: Vertical(g23)
    c: Coincident(g24,g25)
    c: Coincident(g25,g26)
    c: Coincident(g26,g27)
    c: Coincident(g27,g24)
    c: Horizontal(g24)
    c: Horizontal(g26)
    c: Vertical(g25)
    c: Vertical(g27)
    c: Coincident(g28,g29)
    c: Coincident(g29,g30)
    c: Coincident(g30,g31)
    c: Coincident(g31,g28)
    c: Horizontal(g28)
    c: Horizontal(g30)
    c: Vertical(g29)
    c: Vertical(g31)
    c: Equal(g31,g17)
    c: Equal(g17,g23)
    c: Equal(g17,g25)
    c: Equal(g18,g24)
    c: Equal(g18,g22)
    c: Equal(g18,g28)
    c: Vertical(g28,g20)
    c: Vertical(g16,g24)
    c: Horizontal(g24,g28)
    c: Horizontal(g16,g20)
    c: DistanceX(g16,g20) = 120
    c: DistanceY(g24,g16) = 50
FEATURE [PartDesign::Pocket] Pocket001  label="отверстия лицо"
  BaseFeature = -> Pad001
  Direction = (0,0,-1)
  Length = 5
  Length2 = 5
  Profile = -> Sketch003
  ReferenceAxis = -> Sketch003 [N_Axis]
  Type = 2
FEATURE [Sketcher::SketchObject] Sketch004
  FullyConstrained = false
  MapMode = 5
  Placement = pos=(0,0,-2) rot=(1,0,0;3.14159rad)
  Support = -> [Pocket001]
  sketch-geometry (27):
    g0: LineSegment StartX=41.5 StartY=60.8 StartZ=0 EndX=58.5 EndY=60.8 EndZ=0
    g1: LineSegment StartX=58.5 StartY=60.8 StartZ=0 EndX=58.5 EndY=52.8 EndZ=0
    g2: LineSegment StartX=58.5 StartY=52.8 StartZ=0 EndX=41.5 EndY=52.8 EndZ=0
    g3: LineSegment StartX=41.5 StartY=52.8 StartZ=0 EndX=41.5 EndY=60.8 EndZ=0
    g4: LineSegment StartX=41.5 StartY=10.8 StartZ=0 EndX=58.5 EndY=10.8 EndZ=0
    g5: LineSegment StartX=58.5 StartY=10.8 StartZ=0 EndX=58.5 EndY=2.8 EndZ=0
    g6: LineSegment StartX=58.5 StartY=2.8 StartZ=0 EndX=41.5 EndY=2.8 EndZ=0
    g7: LineSegment StartX=41.5 StartY=2.8 StartZ=0 EndX=41.5 EndY=10.8 EndZ=0
    g8: LineSegment StartX=-11 StartY=60.8 StartZ=0 EndX=-2.5 EndY=60.8 EndZ=0
    g9: LineSegment StartX=-2.5 StartY=60.8 StartZ=0 EndX=-2.5 EndY=52.8 EndZ=0
    g10: LineSegment StartX=-2.5 StartY=52.8 StartZ=0 EndX=-11 EndY=52.8 EndZ=0
    g11: LineSegment StartX=-11 StartY=52.8 StartZ=0 EndX=-11 EndY=60.8 EndZ=0
    g12: LineSegment StartX=102.5 StartY=60.8 StartZ=0 EndX=111 EndY=60.8 EndZ=0
    g13: LineSegment StartX=111 StartY=60.8 StartZ=0 EndX=111 EndY=52.8 EndZ=0
    g14: LineSegment StartX=111 StartY=52.8 StartZ=0 EndX=102.5 EndY=52.8 EndZ=0
    g15: LineSegment StartX=102.5 StartY=52.8 StartZ=0 EndX=102.5 EndY=60.8 EndZ=0
    g16: LineSegment StartX=-11 StartY=10.8 StartZ=0 EndX=-2.5 EndY=10.8 EndZ=0
    g17: LineSegment StartX=-2.5 StartY=10.8 StartZ=0 EndX=-2.5 EndY=2.8 EndZ=0
    g18: LineSegment StartX=-2.5 StartY=2.8 StartZ=0 EndX=-11 EndY=2.8 EndZ=0
    g19: LineSegment StartX=-11 StartY=2.8 StartZ=0 EndX=-11 EndY=10.8 EndZ=0
    g20: LineSegment StartX=102.5 StartY=10.8 StartZ=0 EndX=111 EndY=10.8 EndZ=0
    g21: LineSegment StartX=111 StartY=10.8 StartZ=0 EndX=111 EndY=2.8 EndZ=0
    g22: LineSegment StartX=111 StartY=2.8 StartZ=0 EndX=102.5 EndY=2.8 EndZ=0
    g23: LineSegment StartX=102.5 StartY=2.8 StartZ=0 EndX=102.5 EndY=10.8 EndZ=0
    g24: LineSegment StartX=50 StartY=83.6007 StartZ=0 EndX=50 EndY=2.8 EndZ=0
    g25: LineSegment StartX=41.5 StartY=52.8 StartZ=0 EndX=-2.5 EndY=52.8 EndZ=0
    g26: LineSegment StartX=58.5 StartY=52.8 StartZ=0 EndX=102.5 EndY=52.8 EndZ=0
  constraints (78):
    c: Coincident(g0,g1)
    c: Coincident(g1,g2)
    c: Coincident(g2,g3)
    c: Coincident(g3,g0)
    c: Horizontal(g0)
    c: Horizontal(g2)
    c: Vertical(g1)
    c: Vertical(g3)
    c: Coincident(g4,g5)
    c: Coincident(g5,g6)
    c: Coincident(g6,g7)
    c: Coincident(g7,g4)
    c: Horizontal(g4)
    c: Horizontal(g6)
    c: Vertical(g5)
    c: Vertical(g7)
    c: Coincident(g8,g9)
    c: Coincident(g9,g10)
    c: Coincident(g10,g11)
    c: Coincident(g11,g8)
    c: Horizontal(g8)
    c: Horizontal(g10)
    c: Vertical(g9)
    c: Vertical(g11)
    c: Coincident(g12,g13)
    c: Coincident(g13,g14)
    c: Coincident(g14,g15)
    c: Coincident(g15,g12)
    c: Horizontal(g12)
    c: Horizontal(g14)
    c: Vertical(g13)
    c: Vertical(g15)
    c: Coincident(g16,g17)
    c: Coincident(g17,g18)
    c: Coincident(g18,g19)
    c: Coincident(g19,g16)
    c: Horizontal(g16)
    c: Horizontal(g18)
    c: Vertical(g17)
    c: Vertical(g19)
    c: Coincident(g20,g21)
    c: Coincident(g21,g22)
    c: Coincident(g22,g23)
    c: Coincident(g23,g20)
    c: Horizontal(g20)
    c: Horizontal(g22)
    c: Vertical(g21)
    c: Vertical(g23)
    c: DistanceY(g11,g11) = 8
    c: Equal(g11,g3)
    c: Equal(g11,g15)
    c: Equal(g11,g19)
    c: Equal(g11,g7)
    c: Equal(g11,g23)
    c: Horizontal(g8,g0)
    c: Horizontal(g8,g12)
    c: Horizontal(g16,g4)
    c: Horizontal(g16,g20)
    c: Equal(g8,g16)
    c: Equal(g8,g12)
    c: Equal(g8,g20)
    c: Vertical(g8,g16)
    c: Equal(g0,g4)
    c: Vertical(g0,g4)
    c: Vertical(g12,g20)
    c: DistanceX(g8,g8) = 8.5
    c: Vertical(g24)
    c: DistanceX(g-1,g24) = 50
    c: DistanceY(g-1,g16) = 10.8
    c: DistanceY(g16,g8) = 50
    c: Symmetric(g6,g5,g24)
    c: DistanceX(g0,g0) = 17
    c: Coincident(g25,g2)
    c: Coincident(g25,g9)
    c: DistanceX(g25,g25) = 44
    c: Coincident(g26,g1)
    c: Coincident(g26,g14)
    c: Equal(g25,g26)
FEATURE [PartDesign::Pad] Pad002  label="стойки плат"
  BaseFeature = -> Pocket001
  Direction = (0,0,-1)
  Length = 6.5
  Length2 = 10
  Profile = -> Sketch004
  ReferenceAxis = -> Sketch004 [N_Axis]
  Type = 0
FEATURE [Sketcher::SketchObject] Sketch005
  FullyConstrained = false
  MapMode = 5
  Placement = pos=(0,0,-8.5) rot=(1,0,0;3.14159rad)
  Support = -> [Pad002]
  sketch-geometry (22):
    g0: LineSegment StartX=-6.5 StartY=57.8 StartZ=0 EndX=45.5 EndY=57.8 EndZ=0
    g1: LineSegment StartX=45.5 StartY=57.8 StartZ=0 EndX=45.5 EndY=55.8 EndZ=0
    g2: LineSegment StartX=45.5 StartY=55.8 StartZ=0 EndX=-6.5 EndY=55.8 EndZ=0
    g3: LineSegment StartX=-6.5 StartY=55.8 StartZ=0 EndX=-6.5 EndY=57.8 EndZ=0
    g4: LineSegment StartX=-6.5 StartY=7.8 StartZ=0 EndX=45.5 EndY=7.8 EndZ=0
    g5: LineSegment StartX=45.5 StartY=7.8 StartZ=0 EndX=45.5 EndY=5.8 EndZ=0
    g6: LineSegment StartX=45.5 StartY=5.8 StartZ=0 EndX=-6.5 EndY=5.8 EndZ=0
    g7: LineSegment StartX=-6.5 StartY=5.8 StartZ=0 EndX=-6.5 EndY=7.8 EndZ=0
    g8: LineSegment StartX=54.5 StartY=57.8 StartZ=0 EndX=106.5 EndY=57.8 EndZ=0
    g9: LineSegment StartX=106.5 StartY=57.8 StartZ=0 EndX=106.5 EndY=55.8 EndZ=0
    g10: LineSegment StartX=106.5 StartY=55.8 StartZ=0 EndX=54.5 EndY=55.8 EndZ=0
    g11: LineSegment StartX=54.5 StartY=55.8 StartZ=0 EndX=54.5 EndY=57.8 EndZ=0
    g12: LineSegment StartX=54.5 StartY=7.8 StartZ=0 EndX=106.5 EndY=7.8 EndZ=0
    g13: LineSegment StartX=106.5 StartY=7.8 StartZ=0 EndX=106.5 EndY=5.8 EndZ=0
    g14: LineSegment StartX=106.5 StartY=5.8 StartZ=0 EndX=54.5 EndY=5.8 EndZ=0
    g15: LineSegment StartX=54.5 StartY=5.8 StartZ=0 EndX=54.5 EndY=7.8 EndZ=0
    g16: LineSegment StartX=50 StartY=80.381 StartZ=0 EndX=50 EndY=0 EndZ=0
    g17: LineSegment StartX=45.5 StartY=55.8 StartZ=0 EndX=50 EndY=55.8 EndZ=0
    g18: LineSegment StartX=54.5 StartY=55.8 StartZ=0 EndX=50 EndY=55.8 EndZ=0
    g19: LineSegment StartX=54.5 StartY=5.8 StartZ=0 EndX=50 EndY=5.8 EndZ=0
    g20: LineSegment StartX=45.5 StartY=5.8 StartZ=0 EndX=50 EndY=5.8 EndZ=0
    g21: GeomPoint X=41.5493 Y=2.79623 Z=0
  constraints (61):
    c: Coincident(g0,g1)
    c: Coincident(g1,g2)
    c: Coincident(g2,g3)
    c: Coincident(g3,g0)
    c: Horizontal(g0)
    c: Horizontal(g2)
    c: Vertical(g1)
    c: Vertical(g3)
    c: Coincident(g4,g5)
    c: Coincident(g5,g6)
    c: Coincident(g6,g7)
    c: Coincident(g7,g4)
    c: Horizontal(g4)
    c: Horizontal(g6)
    c: Vertical(g5)
    c: Vertical(g7)
    c: Coincident(g8,g9)
    c: Coincident(g9,g10)
    c: Coincident(g10,g11)
    c: Coincident(g11,g8)
    c: Horizontal(g8)
    c: Horizontal(g10)
    c: Vertical(g9)
    c: Vertical(g11)
    c: Coincident(g12,g13)
    c: Coincident(g13,g14)
    c: Coincident(g14,g15)
    c: Coincident(g15,g12)
    c: Horizontal(g12)
    c: Horizontal(g14)
    c: Vertical(g13)
    c: Vertical(g15)
    c: DistanceY(g3,g3) = 2
    c: Equal(g3,g11)
    c: Equal(g3,g7)
    c: Equal(g3,g15)
    c: Equal(g0,g4)
    c: Equal(g0,g8)
    c: Equal(g0,g12)
    c: DistanceX(g0,g0) = 52
    c: PointOnObject(g16,g-1)
    c: Vertical(g16)
    c: DistanceX(g-1,g16) = 50
    c: Coincident(g17,g1)
    c: PointOnObject(g17,g16)
    c: Horizontal(g17)
    c: Coincident(g18,g10)
    c: Horizontal(g18)
    c: Coincident(g19,g14)
    c: PointOnObject(g19,g16)
    c: Horizontal(g19)
    c: Coincident(g20,g5)
    c: Horizontal(g20)
    c: Coincident(g20,g19)
    c: Coincident(g18,g17)
    c: Equal(g17,g18)
    c: Equal(g17,g20)
    c: Equal(g17,g19)
    c: DistanceX(g17,g17) = 4.5
    c: DistanceY(g19,g17) = 50
    c: DistanceY(g16,g19) = 5.8
FEATURE [PartDesign::Pocket] Pocket002  label="прорезь для плат"
  BaseFeature = -> Pad002
  Direction = (0,0,1)
  Length = 3.9
  Length2 = 5
  Profile = -> Sketch005
  ReferenceAxis = -> Sketch005 [N_Axis]
  Type = 0
FEATURE [Sketcher::SketchObject] Sketch006
  ExternalGeometry = -> [Pocket002]
  FullyConstrained = true
  MapMode = 5
  Placement = pos=(-20,0,0) rot=(0.57735,-0.57735,-0.57735;2.0944rad)
  Support = -> [Pocket002]
  sketch-geometry (8):
    g0: LineSegment StartX=9 StartY=-14 StartZ=0 EndX=9 EndY=-18 EndZ=0
    g1: LineSegment StartX=12 StartY=-14 StartZ=0 EndX=12 EndY=-18 EndZ=0
    g2: ArcOfCircle CenterX=10.5 CenterY=-14 CenterZ=0 NormalX=0 NormalY=0 NormalZ=1 AngleXU=0 Radius=1.5 StartAngle=0 EndAngle=3.14159
    g3: LineSegment StartX=9 StartY=-18 StartZ=0 EndX=12 EndY=-18 EndZ=0
    g4: LineSegment StartX=59 StartY=-14 StartZ=0 EndX=59 EndY=-18 EndZ=0
    g5: LineSegment StartX=62 StartY=-18 StartZ=0 EndX=62 EndY=-14 EndZ=0
    g6: ArcOfCircle CenterX=60.5 CenterY=-14 CenterZ=0 NormalX=0 NormalY=0 NormalZ=1 AngleXU=0 Radius=1.5 StartAngle=2e-16 EndAngle=3.14159
    g7: LineSegment StartX=59 StartY=-18 StartZ=0 EndX=62 EndY=-18 EndZ=0
  constraints (26):
    c: PointOnObject(g0,g-3)
    c: Vertical(g0)
    c: PointOnObject(g1,g-3)
    c: Vertical(g1)
    c: Coincident(g2,g0)
    c: Coincident(g2,g1)
    c: Horizontal(g0,g2)
    c: Horizontal(g0,g1)
    c: DistanceY(g0,g0) = 4
    c: Diameter(g2) = 3
    c: Coincident(g3,g0)
    c: Coincident(g3,g1)
    c: PointOnObject(g4,g-3)
    c: Vertical(g4)
    c: PointOnObject(g5,g-3)
    c: Vertical(g5)
    c: Coincident(g6,g4)
    c: Coincident(g6,g5)
    c: Horizontal(g4,g6)
    c: Horizontal(g4,g5)
    c: Equal(g2,g6)
    c: Equal(g0,g4)
    c: DistanceX(g0,g4) = 50
    c: Distance(g0,g-2) = 9
    c: Coincident(g7,g4)
    c: Coincident(g7,g5)
FEATURE [PartDesign::Pocket] Pocket003  label="отверстия под провода"
  BaseFeature = -> Pocket002
  Direction = (1,0,0)
  Length = 5
  Length2 = 5
  Profile = -> Sketch006
  ReferenceAxis = -> Sketch006 [N_Axis]
  Type = 1
FEATURE [Sketcher::SketchObject] Sketch007
  FullyConstrained = true
  MapMode = 5
  Support = -> [XY_Plane022]
  sketch-geometry (4):
    g0: LineSegment StartX=-20 StartY=33 StartZ=0 EndX=120 EndY=33 EndZ=0
    g1: LineSegment StartX=120 StartY=33 StartZ=0 EndX=120 EndY=-77 EndZ=0
    g2: LineSegment StartX=120 StartY=-77 StartZ=0 EndX=-20 EndY=-77 EndZ=0
    g3: LineSegment StartX=-20 StartY=-77 StartZ=0 EndX=-20 EndY=33 EndZ=0
  constraints (12):
    c: Coincident(g0,g1)
    c: Coincident(g1,g2)
    c: Coincident(g2,g3)
    c: Coincident(g3,g0)
    c: Horizontal(g0)
    c: Horizontal(g2)
    c: Vertical(g1)
    c: Vertical(g3)
    c: DistanceX(g0,g0) = 140
    c: DistanceY(g3,g3) = 110
    c: DistanceX(g0,g-1) = 20
    c: DistanceY(g-1,g0) = 33
FEATURE [PartDesign::Pad] Pad003  label="коробка001"
  Direction = (0,0,1)
  Length = 20
  Length2 = 10
  Profile = -> Sketch007
  ReferenceAxis = -> Sketch007 [N_Axis]
  Type = 0
FEATURE [Sketcher::SketchObject] Sketch008
  FullyConstrained = true
  MapMode = 5
  Placement = pos=(0,0,20) rot=(0,0,1;0rad)
  Support = -> [Pad003]
  sketch-geometry (4):
    g0: LineSegment StartX=-18 StartY=31 StartZ=0 EndX=118 EndY=31 EndZ=0
    g1: LineSegment StartX=118 StartY=31 StartZ=0 EndX=118 EndY=-75 EndZ=0
    g2: LineSegment StartX=118 StartY=-75 StartZ=0 EndX=-18 EndY=-75 EndZ=0
    g3: LineSegment StartX=-18 StartY=-75 StartZ=0 EndX=-18 EndY=31 EndZ=0
  constraints (12):
    c: Coincident(g0,g1)
    c: Coincident(g1,g2)
    c: Coincident(g2,g3)
    c: Coincident(g3,g0)
    c: Horizontal(g0)
    c: Horizontal(g2)
    c: Vertical(g1)
    c: Vertical(g3)
    c: DistanceX(g0,g0) = 136
    c: DistanceY(g3,g3) = 106
    c: DistanceX(g2,g-1) = 18
    c: Distance(g0,g-1) = 31
FEATURE [PartDesign::Pocket] Pocket004  label="глубина001"
  BaseFeature = -> Pad003
  Direction = (0,0,-1)
  Length = 18
  Length2 = 5
  Profile = -> Sketch008
  ReferenceAxis = -> Sketch008 [N_Axis]
  Type = 0
FEATURE [Sketcher::SketchObject] Sketch009
  FullyConstrained = false
  MapMode = 5
  Placement = pos=(0,0,2) rot=(0,0,1;0rad)
  Support = -> [Pocket004]
  sketch-geometry (7):
    g0: Circle CenterX=39.5 CenterY=-70 CenterZ=0 NormalX=0 NormalY=0 NormalZ=1 AngleXU=0 Radius=4
    g1: Circle CenterX=60.5 CenterY=-70 CenterZ=0 NormalX=0 NormalY=0 NormalZ=1 AngleXU=0 Radius=4
    g2: LineSegment StartX=50 StartY=-52.8757 StartZ=0 EndX=50 EndY=-81.9341 EndZ=0
    g3: LineSegment StartX=39.5 StartY=-70 StartZ=0 EndX=50 EndY=-70 EndZ=0
    g4: LineSegment StartX=50 StartY=-70 StartZ=0 EndX=60.5 EndY=-70 EndZ=0
    g5: Circle CenterX=39.5 CenterY=-70 CenterZ=0 NormalX=0 NormalY=0 NormalZ=1 AngleXU=0 Radius=1.1
    g6: Circle CenterX=60.5 CenterY=-70 CenterZ=0 NormalX=0 NormalY=0 NormalZ=1 AngleXU=0 Radius=1.1
  constraints (17):
    c: Equal(g0,g1)
    c: Diameter(g0) = 8
    c: Horizontal(g0,g1)
    c: Vertical(g2)
    c: DistanceX(g-1,g2) = 50
    c: Coincident(g3,g0)
    c: PointOnObject(g3,g2)
    c: Horizontal(g3)
    c: Coincident(g4,g3)
    c: Coincident(g4,g1)
    c: Equal(g3,g4)
    c: DistanceX(g3,g3) = 10.5
    c: DistanceY(g0,g-1) = 70
    c: Coincident(g5,g0)
    c: Coincident(g6,g1)
    c: Equal(g5,g6)
    c: Diameter(g5) = 2.2
FEATURE [PartDesign::Pad] Pad004  label="крепление dc-разъёма"
  BaseFeature = -> Pocket004
  Direction = (0,0,1)
  Length = 3
  Length2 = 10
  Profile = -> Sketch009
  ReferenceAxis = -> Sketch009 [N_Axis]
  Type = 0
FEATURE [Sketcher::SketchObject] Sketch010
  ExternalGeometry = -> [Pad004]
  FullyConstrained = true
  MapMode = 5
  Placement = pos=(0,0,2) rot=(0,0,1;0rad)
  Support = -> [Pad004]
  sketch-geometry (24):
    g0: LineSegment StartX=110 StartY=-71 StartZ=0 EndX=110 EndY=-75 EndZ=0
    g1: LineSegment StartX=110 StartY=-75 StartZ=0 EndX=118 EndY=-75 EndZ=0
    g2: LineSegment StartX=118 StartY=-75 StartZ=0 EndX=118 EndY=-67 EndZ=0
    g3: LineSegment StartX=118 StartY=-67 StartZ=0 EndX=114 EndY=-67 EndZ=0
    g4: LineSegment StartX=-14 StartY=-67 StartZ=0 EndX=-18 EndY=-67 EndZ=0
    g5: LineSegment StartX=-18 StartY=-67 StartZ=0 EndX=-18 EndY=-75 EndZ=0
    g6: LineSegment StartX=-10 StartY=-75 StartZ=0 EndX=-10 EndY=-71 EndZ=0
    g7: LineSegment StartX=-10 StartY=27 StartZ=0 EndX=-10 EndY=31 EndZ=0
    g8: LineSegment StartX=-10 StartY=31 StartZ=0 EndX=-18 EndY=31 EndZ=0
    g9: LineSegment StartX=-18 StartY=31 StartZ=0 EndX=-18 EndY=23 EndZ=0
    g10: LineSegment StartX=-18 StartY=23 StartZ=0 EndX=-14 EndY=23 EndZ=0
    g11: LineSegment StartX=110 StartY=27 StartZ=0 EndX=110 EndY=31 EndZ=0
    g12: LineSegment StartX=110 StartY=31 StartZ=0 EndX=118 EndY=31 EndZ=0
    g13: LineSegment StartX=118 StartY=31 StartZ=0 EndX=118 EndY=23 EndZ=0
    g14: LineSegment StartX=118 StartY=23 StartZ=0 EndX=114 EndY=23 EndZ=0
    g15: ArcOfCircle CenterX=114 CenterY=27 CenterZ=0 NormalX=0 NormalY=0 NormalZ=1 AngleXU=0 Radius=4 StartAngle=3.14159 EndAngle=4.71239
    g16: ArcOfCircle CenterX=-14 CenterY=27 CenterZ=0 NormalX=0 NormalY=0 NormalZ=1 AngleXU=0 Radius=4 StartAngle=4.71239 EndAngle=6.28319
    g17: ArcOfCircle CenterX=-14 CenterY=-71 CenterZ=0 NormalX=0 NormalY=0 NormalZ=1 AngleXU=0 Radius=4 StartAngle=-9e-16 EndAngle=1.5708
    g18: ArcOfCircle CenterX=114 CenterY=-71 CenterZ=0 NormalX=0 NormalY=0 NormalZ=1 AngleXU=0 Radius=4 StartAngle=1.5708 EndAngle=3.14159
    g19: LineSegment StartX=-18 StartY=-75 StartZ=0 EndX=-10 EndY=-75 EndZ=0
    g20: Circle CenterX=-14 CenterY=27 CenterZ=0 NormalX=0 NormalY=0 NormalZ=1 AngleXU=0 Radius=1.6
    g21: Circle CenterX=114 CenterY=27 CenterZ=0 NormalX=0 NormalY=0 NormalZ=1 AngleXU=0 Radius=1.6
    g22: Circle CenterX=114 CenterY=-71 CenterZ=0 NormalX=0 NormalY=0 NormalZ=1 AngleXU=0 Radius=1.6
    g23: Circle CenterX=-14 CenterY=-71 CenterZ=0 NormalX=0 NormalY=0 NormalZ=1 AngleXU=0 Radius=1.6
  constraints (68):
    c: Vertical(g0)
    c: Coincident(g1,g0)
    c: Coincident(g1,g-6)
    c: Horizontal(g1)
    c: Coincident(g2,g1)
    c: Vertical(g2)
    c: Horizontal(g3)
    c: Horizontal(g4)
    c: Coincident(g5,g-5)
    c: Vertical(g5)
    c: Vertical(g6)
    c: Vertical(g7)
    c: Coincident(g8,g-3)
    c: Horizontal(g8)
    c: Coincident(g9,g8)
    c: Vertical(g9)
    c: Horizontal(g10)
    c: Vertical(g11)
    c: Coincident(g12,g-4)
    c: Horizontal(g12)
    c: Coincident(g13,g12)
    c: Vertical(g13)
    c: Coincident(g14,g13)
    c: Horizontal(g14)
    c: Coincident(g15,g14)
    c: Coincident(g15,g11)
    c: Coincident(g16,g10)
    c: Coincident(g16,g7)
    c: Coincident(g17,g4)
    c: Coincident(g17,g6)
    c: Coincident(g18,g0)
    c: Coincident(g18,g3)
    c: Horizontal(g16,g7)
    c: Horizontal(g16,g15)
    c: Horizontal(g15,g11)
    c: Horizontal(g18,g0)
    c: Horizontal(g18,g17)
    c: Horizontal(g17,g6)
    c: Vertical(g17,g4)
    c: Vertical(g17,g16)
    c: Vertical(g16,g10)
    c: Vertical(g15,g14)
    c: Vertical(g15,g18)
    c: Vertical(g18,g3)
    c: Equal(g0,g3)
    c: Coincident(g3,g2)
    c: Equal(g3,g7)
    c: Equal(g7,g10)
    c: Equal(g6,g4)
    c: Equal(g16,g15)
    c: Equal(g16,g17)
    c: Equal(g16,g18)
    c: DistanceY(g7,g7) = 4
    c: Radius(g16) = 4
    c: Coincident(g10,g9)
    c: Coincident(g12,g11)
    c: Coincident(g5,g4)
    c: Coincident(g8,g7)
    c: Coincident(g19,g5)
    c: Coincident(g19,g6)
    c: Coincident(g20,g16)
    c: Coincident(g21,g15)
    c: Coincident(g22,g18)
    c: Coincident(g23,g17)
    c: Equal(g23,g20)
    c: Equal(g20,g21)
    c: Equal(g20,g22)
    c: Diameter(g20) = 3.2
FEATURE [PartDesign::Pad] Pad005  label="винты"
  BaseFeature = -> Pad004
  Direction = (0,0,1)
  Length = 13.6
  Length2 = 10
  Profile = -> Sketch010
  ReferenceAxis = -> Sketch010 [N_Axis]
  Type = 0
FEATURE [Sketcher::SketchObject] Sketch011
  ExternalGeometry = -> [Pad005]
  FullyConstrained = true
  MapMode = 5
  Placement = pos=(0,0,0) rot=(1,0,0;3.14159rad)
  Support = -> [Pad005]
  sketch-geometry (8):
    g0: LineSegment StartX=-14 StartY=71 StartZ=0 EndX=114 EndY=71 EndZ=0
    g1: LineSegment StartX=114 StartY=71 StartZ=0 EndX=114 EndY=-27 EndZ=0
    g2: LineSegment StartX=114 StartY=-27 StartZ=0 EndX=-14 EndY=-27 EndZ=0
    g3: LineSegment StartX=-14 StartY=-27 StartZ=0 EndX=-14 EndY=71 EndZ=0
    g4: Circle CenterX=-14 CenterY=71 CenterZ=0 NormalX=0 NormalY=0 NormalZ=1 AngleXU=0 Radius=3
    g5: Circle CenterX=114 CenterY=71 CenterZ=0 NormalX=0 NormalY=0 NormalZ=1 AngleXU=0 Radius=3
    g6: Circle CenterX=-14 CenterY=-27 CenterZ=0 NormalX=0 NormalY=0 NormalZ=1 AngleXU=0 Radius=3
    g7: Circle CenterX=114 CenterY=-27 CenterZ=0 NormalX=0 NormalY=0 NormalZ=1 AngleXU=0 Radius=3
  constraints (20):
    c: Coincident(g0,g1)
    c: Coincident(g1,g2)
    c: Coincident(g2,g3)
    c: Coincident(g3,g0)
    c: Horizontal(g0)
    c: Horizontal(g2)
    c: Vertical(g1)
    c: Vertical(g3)
    c: DistanceX(g0,g0) = 128
    c: DistanceX(g-3,g0) = 6
    c: DistanceY(g0,g-3) = 6
    c: DistanceY(g3,g3) = 98
    c: Coincident(g4,g0)
    c: Coincident(g5,g0)
    c: Coincident(g6,g2)
    c: Coincident(g7,g1)
    c: Equal(g4,g5)
    c: Equal(g4,g7)
    c: Equal(g4,g6)
    c: Diameter(g4) = 6
FEATURE [PartDesign::Pocket] Pocket005  label="углубления винтов"
  BaseFeature = -> Pad005
  Direction = (0,0,1)
  Length = 10
  Length2 = 5
  Profile = -> Sketch011
  ReferenceAxis = -> Sketch011 [N_Axis]
  Type = 0
FEATURE [Sketcher::SketchObject] Sketch012
  ExternalGeometry = -> [Pocket005]
  FullyConstrained = true
  MapMode = 5
  Placement = pos=(0,-77,0) rot=(1,0,0;1.5708rad)
  Support = -> [Pocket005]
  sketch-geometry (4):
    g0: LineSegment StartX=45.1 StartY=20 StartZ=0 EndX=54.9 EndY=20 EndZ=0
    g1: LineSegment StartX=54.9 StartY=20 StartZ=0 EndX=54.9 EndY=6.4 EndZ=0
    g2: LineSegment StartX=54.9 StartY=6.4 StartZ=0 EndX=45.1 EndY=6.4 EndZ=0
    g3: LineSegment StartX=45.1 StartY=6.4 StartZ=0 EndX=45.1 EndY=20 EndZ=0
  constraints (12):
    c: Coincident(g0,g1)
    c: Coincident(g1,g2)
    c: Coincident(g2,g3)
    c: Coincident(g3,g0)
    c: Horizontal(g0)
    c: Horizontal(g2)
    c: Vertical(g1)
    c: Vertical(g3)
    c: DistanceX(g2,g2) = 9.8
    c: DistanceY(g3,g3) = 13.6
    c: PointOnObject(g0,g-3)
    c: DistanceX(g-1,g0) = 45.1
FEATURE [PartDesign::Pocket] Pocket006  label="отверстие под dc"
  BaseFeature = -> Pocket005
  Direction = (0,1,-2e-16)
  Length = 5
  Length2 = 5
  Profile = -> Sketch012
  ReferenceAxis = -> Sketch012 [N_Axis]
  Type = 2
FEATURE [Sketcher::SketchObject] Sketch013
  ExternalGeometry = -> [Pocket003]
  FullyConstrained = true
  MapMode = 5
  Placement = pos=(0,0,-18) rot=(1,0,0;3.14159rad)
  Support = -> [Pocket003]
  sketch-geometry (4):
    g0: LineSegment StartX=45.3 StartY=77 StartZ=0 EndX=54.7 EndY=77 EndZ=0
    g1: LineSegment StartX=54.7 StartY=77 StartZ=0 EndX=54.7 EndY=75 EndZ=0
    g2: LineSegment StartX=54.7 StartY=75 StartZ=0 EndX=45.3 EndY=75 EndZ=0
    g3: LineSegment StartX=45.3 StartY=75 StartZ=0 EndX=45.3 EndY=77 EndZ=0
  constraints (12):
    c: Coincident(g0,g1)
    c: Coincident(g1,g2)
    c: Coincident(g2,g3)
    c: Coincident(g3,g0)
    c: Horizontal(g0)
    c: Horizontal(g2)
    c: Vertical(g1)
    c: Vertical(g3)
    c: PointOnObject(g0,g-3)
    c: DistanceY(g3,g3) = 2
    c: DistanceX(g0,g0) = 9.4
    c: Distance(g0,g-2) = 45.3
FEATURE [PartDesign::Pad] Pad006  label="заглушка dc"
  BaseFeature = -> Pocket003
  Direction = (0,0,-1)
  Length = 2
  Length2 = 10
  Profile = -> Sketch013
  ReferenceAxis = -> Sketch013 [N_Axis]
  Type = 0
FEATURE [Sketcher::SketchObject] Sketch014
  FullyConstrained = false
  MapMode = 5
  Placement = pos=(0,0,2) rot=(0,0,1;0rad)
  Support = -> [Pocket006]
  sketch-geometry (27):
    g0: LineSegment StartX=41.5 StartY=-2.8 StartZ=0 EndX=58.5 EndY=-2.8 EndZ=0
    g1: LineSegment StartX=58.5 StartY=-2.8 StartZ=0 EndX=58.5 EndY=-10.8 EndZ=0
    g2: LineSegment StartX=58.5 StartY=-10.8 StartZ=0 EndX=41.5 EndY=-10.8 EndZ=0
    g3: LineSegment StartX=41.5 StartY=-10.8 StartZ=0 EndX=41.5 EndY=-2.8 EndZ=0
    g4: LineSegment StartX=41.5 StartY=-52.8 StartZ=0 EndX=58.5 EndY=-52.8 EndZ=0
    g5: LineSegment StartX=58.5 StartY=-52.8 StartZ=0 EndX=58.5 EndY=-60.8 EndZ=0
    g6: LineSegment StartX=58.5 StartY=-60.8 StartZ=0 EndX=41.5 EndY=-60.8 EndZ=0
    g7: LineSegment StartX=41.5 StartY=-60.8 StartZ=0 EndX=41.5 EndY=-52.8 EndZ=0
    g8: LineSegment StartX=-11 StartY=-2.8 StartZ=0 EndX=-2.5 EndY=-2.8 EndZ=0
    g9: LineSegment StartX=-2.5 StartY=-2.8 StartZ=0 EndX=-2.5 EndY=-10.8 EndZ=0
    g10: LineSegment StartX=-2.5 StartY=-10.8 StartZ=0 EndX=-11 EndY=-10.8 EndZ=0
    g11: LineSegment StartX=-11 StartY=-10.8 StartZ=0 EndX=-11 EndY=-2.8 EndZ=0
    g12: LineSegment StartX=102.5 StartY=-2.8 StartZ=0 EndX=111 EndY=-2.8 EndZ=0
    g13: LineSegment StartX=111 StartY=-2.8 StartZ=0 EndX=111 EndY=-10.8 EndZ=0
    g14: LineSegment StartX=111 StartY=-10.8 StartZ=0 EndX=102.5 EndY=-10.8 EndZ=0
    g15: LineSegment StartX=102.5 StartY=-10.8 StartZ=0 EndX=102.5 EndY=-2.8 EndZ=0
    g16: LineSegment StartX=-11 StartY=-52.8 StartZ=0 EndX=-2.5 EndY=-52.8 EndZ=0
    g17: LineSegment StartX=-2.5 StartY=-52.8 StartZ=0 EndX=-2.5 EndY=-60.8 EndZ=0
    g18: LineSegment StartX=-2.5 StartY=-60.8 StartZ=0 EndX=-11 EndY=-60.8 EndZ=0
    g19: LineSegment StartX=-11 StartY=-60.8 StartZ=0 EndX=-11 EndY=-52.8 EndZ=0
    g20: LineSegment StartX=102.5 StartY=-52.8 StartZ=0 EndX=111 EndY=-52.8 EndZ=0
    g21: LineSegment StartX=111 StartY=-52.8 StartZ=0 EndX=111 EndY=-60.8 EndZ=0
    g22: LineSegment StartX=111 StartY=-60.8 StartZ=0 EndX=102.5 EndY=-60.8 EndZ=0
    g23: LineSegment StartX=102.5 StartY=-60.8 StartZ=0 EndX=102.5 EndY=-52.8 EndZ=0
    g24: LineSegment StartX=50 StartY=83.6007 StartZ=0 EndX=50 EndY=-60.8 EndZ=0
    g25: LineSegment StartX=41.5 StartY=-10.8 StartZ=0 EndX=-2.5 EndY=-10.8 EndZ=0
    g26: LineSegment StartX=58.5 StartY=-10.8 StartZ=0 EndX=102.5 EndY=-10.8 EndZ=0
  constraints (77):
    c: Coincident(g0,g1)
    c: Coincident(g1,g2)
    c: Coincident(g2,g3)
    c: Coincident(g3,g0)
    c: Horizontal(g0)
    c: Horizontal(g2)
    c: Vertical(g1)
    c: Vertical(g3)
    c: Coincident(g4,g5)
    c: Coincident(g5,g6)
    c: Coincident(g6,g7)
    c: Coincident(g7,g4)
    c: Horizontal(g4)
    c: Horizontal(g6)
    c: Vertical(g5)
    c: Vertical(g7)
    c: Coincident(g8,g9)
    c: Coincident(g9,g10)
    c: Coincident(g10,g11)
    c: Coincident(g11,g8)
    c: Horizontal(g8)
    c: Horizontal(g10)
    c: Vertical(g9)
    c: Vertical(g11)
    c: Coincident(g12,g13)
    c: Coincident(g13,g14)
    c: Coincident(g14,g15)
    c: Coincident(g15,g12)
    c: Horizontal(g12)
    c: Horizontal(g14)
    c: Vertical(g13)
    c: Vertical(g15)
    c: Coincident(g16,g17)
    c: Coincident(g17,g18)
    c: Coincident(g18,g19)
    c: Coincident(g19,g16)
    c: Horizontal(g16)
    c: Horizontal(g18)
    c: Vertical(g17)
    c: Coincident(g20,g21)
    c: Coincident(g21,g22)
    c: Coincident(g22,g23)
    c: Coincident(g23,g20)
    c: Horizontal(g20)
    c: Horizontal(g22)
    c: Vertical(g21)
    c: Vertical(g23)
    c: DistanceY(g11,g11) = 8
    c: Equal(g11,g3)
    c: Equal(g11,g15)
    c: Equal(g11,g19)
    c: Equal(g11,g7)
    c: Equal(g11,g23)
    c: Horizontal(g8,g0)
    c: Horizontal(g8,g12)
    c: Horizontal(g16,g4)
    c: Horizontal(g16,g20)
    c: Equal(g8,g16)
    c: Equal(g8,g12)
    c: Equal(g8,g20)
    c: Vertical(g8,g16)
    c: Equal(g0,g4)
    c: Vertical(g0,g4)
    c: Vertical(g12,g20)
    c: DistanceX(g8,g8) = 8.5
    c: Vertical(g24)
    c: DistanceX(g-1,g24) = 50
    c: DistanceY(g16,g8) = 50
    c: Symmetric(g6,g5,g24)
    c: DistanceX(g0,g0) = 17
    c: Coincident(g25,g2)
    c: Coincident(g25,g9)
    c: DistanceX(g25,g25) = 44
    c: Coincident(g26,g1)
    c: Coincident(g26,g14)
    c: Equal(g25,g26)
    c: DistanceY(g10,g-1) = 10.8
FEATURE [PartDesign::Pad] Pad007  label="стойки плат001"
  BaseFeature = -> Pocket006
  Direction = (0,0,1)
  Length = 8.5
  Length2 = 10
  Profile = -> Sketch014
  ReferenceAxis = -> Sketch014 [N_Axis]
  Type = 0
FEATURE [Sketcher::SketchObject] Sketch015
  FullyConstrained = false
  MapMode = 5
  Placement = pos=(0,0,10.5) rot=(0,0,1;0rad)
  Support = -> [Pad007]
  sketch-geometry (22):
    g0: LineSegment StartX=-6.5 StartY=-5.8 StartZ=0 EndX=45.5 EndY=-5.8 EndZ=0
    g1: LineSegment StartX=45.5 StartY=-5.8 StartZ=0 EndX=45.5 EndY=-7.8 EndZ=0
    g2: LineSegment StartX=45.5 StartY=-7.8 StartZ=0 EndX=-6.5 EndY=-7.8 EndZ=0
    g3: LineSegment StartX=-6.5 StartY=-7.8 StartZ=0 EndX=-6.5 EndY=-5.8 EndZ=0
    g4: LineSegment StartX=-6.5 StartY=-55.8 StartZ=0 EndX=45.5 EndY=-55.8 EndZ=0
    g5: LineSegment StartX=45.5 StartY=-55.8 StartZ=0 EndX=45.5 EndY=-57.8 EndZ=0
    g6: LineSegment StartX=45.5 StartY=-57.8 StartZ=0 EndX=-6.5 EndY=-57.8 EndZ=0
    g7: LineSegment StartX=-6.5 StartY=-57.8 StartZ=0 EndX=-6.5 EndY=-55.8 EndZ=0
    g8: LineSegment StartX=54.5 StartY=-5.8 StartZ=0 EndX=106.5 EndY=-5.8 EndZ=0
    g9: LineSegment StartX=106.5 StartY=-5.8 StartZ=0 EndX=106.5 EndY=-7.8 EndZ=0
    g10: LineSegment StartX=106.5 StartY=-7.8 StartZ=0 EndX=54.5 EndY=-7.8 EndZ=0
    g11: LineSegment StartX=54.5 StartY=-7.8 StartZ=0 EndX=54.5 EndY=-5.8 EndZ=0
    g12: LineSegment StartX=54.5 StartY=-55.8 StartZ=0 EndX=106.5 EndY=-55.8 EndZ=0
    g13: LineSegment StartX=106.5 StartY=-55.8 StartZ=0 EndX=106.5 EndY=-57.8 EndZ=0
    g14: LineSegment StartX=106.5 StartY=-57.8 StartZ=0 EndX=54.5 EndY=-57.8 EndZ=0
    g15: LineSegment StartX=54.5 StartY=-57.8 StartZ=0 EndX=54.5 EndY=-55.8 EndZ=0
    g16: LineSegment StartX=50 StartY=-7.8 StartZ=0 EndX=50 EndY=0 EndZ=0
    g17: LineSegment StartX=45.5 StartY=-7.8 StartZ=0 EndX=50 EndY=-7.8 EndZ=0
    g18: LineSegment StartX=54.5 StartY=-7.8 StartZ=0 EndX=50 EndY=-7.8 EndZ=0
    g19: LineSegment StartX=54.5 StartY=-57.8 StartZ=0 EndX=50 EndY=-57.8 EndZ=0
    g20: LineSegment StartX=45.5 StartY=-57.8 StartZ=0 EndX=50 EndY=-57.8 EndZ=0
    g21: GeomPoint X=41.5493 Y=2.79623 Z=0
  constraints (59):
    c: Coincident(g0,g1)
    c: Coincident(g1,g2)
    c: Coincident(g2,g3)
    c: Coincident(g3,g0)
    c: Horizontal(g0)
    c: Horizontal(g2)
    c: Vertical(g1)
    c: Vertical(g3)
    c: Coincident(g4,g5)
    c: Coincident(g5,g6)
    c: Coincident(g6,g7)
    c: Coincident(g7,g4)
    c: Horizontal(g4)
    c: Horizontal(g6)
    c: Vertical(g7)
    c: Coincident(g8,g9)
    c: Coincident(g9,g10)
    c: Coincident(g10,g11)
    c: Coincident(g11,g8)
    c: Horizontal(g8)
    c: Horizontal(g10)
    c: Vertical(g9)
    c: Vertical(g11)
    c: Coincident(g12,g13)
    c: Coincident(g13,g14)
    c: Coincident(g14,g15)
    c: Coincident(g15,g12)
    c: Horizontal(g12)
    c: Horizontal(g14)
    c: Vertical(g13)
    c: DistanceY(g3,g3) = 2
    c: Equal(g3,g11)
    c: Equal(g3,g7)
    c: Equal(g3,g15)
    c: Equal(g0,g4)
    c: Equal(g0,g8)
    c: Equal(g0,g12)
    c: DistanceX(g0,g0) = 52
    c: PointOnObject(g16,g-1)
    c: Vertical(g16)
    c: DistanceX(g-1,g16) = 50
    c: Coincident(g17,g1)
    c: Horizontal(g17)
    c: Coincident(g18,g10)
    c: Horizontal(g18)
    c: Coincident(g19,g14)
    c: PointOnObject(g19,g16)
    c: Horizontal(g19)
    c: Coincident(g20,g5)
    c: Horizontal(g20)
    c: Coincident(g20,g19)
    c: Coincident(g18,g17)
    c: Equal(g17,g18)
    c: Equal(g17,g20)
    c: Equal(g17,g19)
    c: DistanceX(g17,g17) = 4.5
    c: DistanceY(g19,g17) = 50
    c: Coincident(g16,g17)
    c: DistanceY(g16,g16) = 7.8
FEATURE [PartDesign::Pocket] Pocket007  label="прорезь для плат001"
  BaseFeature = -> Pad007
  Direction = (0,0,-1)
  Length = 3.9
  Length2 = 5
  Profile = -> Sketch015
  ReferenceAxis = -> Sketch015 [N_Axis]
  Type = 0
FEATURE [PartDesign::Fillet] Fillet  label="сглаж внутр001"
  Base = -> Pocket007 [Edge61,Edge58,Edge49,Edge43,Edge53,Edge52,Edge46,Edge40,Edge179,Edge182,Edge197,Edge198,Edge213,Edge214,Edge135,Edge138,Edge157,Edge158,Edge173,Edge174,Edge136,Edge145,Edge151,Edge165,Edge167,Edge176,Edge180,Edge189,Edge191,Edge205,Edge207,Edge216]
  BaseFeature = -> Pocket007
  Radius = 2
  SupportTransform = false
  UseAllEdges = false
FEATURE [PartDesign::Fillet] Fillet001  label="сглаж рёбра001"
  Base = -> Fillet [Edge48,Edge45,Edge56,Edge42]
  BaseFeature = -> Fillet
  Radius = 4
  SupportTransform = false
  UseAllEdges = false
FEATURE [PartDesign::Fillet] Fillet002  label="сглаж низ"
  Base = -> Fillet001 [Edge62]
  BaseFeature = -> Fillet001
  Radius = 2
  SupportTransform = false
  UseAllEdges = false
FEATURE [PartDesign::Body] Body001  label="down"
  Group = -> [Sketch007,Pad003,Sketch008,Pocket004,Sketch009,Pad004,Sketch010,Pad005,Sketch011,Pocket005,Sketch012,Pocket006,Sketch014,Pad007,Sketch015,Pocket007,Fillet,Fillet001,Fillet002]
  Origin = -> Origin022
  Placement = pos=(0,0,-23) rot=(0,0,1;0rad)
  Tip = -> Fillet002
FEATURE [Sketcher::SketchObject] Sketch016
  ExternalGeometry = -> [Pad006]
  FullyConstrained = true
  MapMode = 5
  Placement = pos=(0,0,-18) rot=(1,0,0;3.14159rad)
  Support = -> [Pad006]
  sketch-geometry (16):
    g0: LineSegment StartX=-20 StartY=77 StartZ=0 EndX=120 EndY=77 EndZ=0
    g1: LineSegment StartX=120 StartY=77 StartZ=0 EndX=120 EndY=-33 EndZ=0
    g2: LineSegment StartX=120 StartY=-33 StartZ=0 EndX=-20 EndY=-33 EndZ=0
    g3: LineSegment StartX=-20 StartY=-33 StartZ=0 EndX=-20 EndY=77 EndZ=0
    g4: LineSegment StartX=-17.7 StartY=74.7 StartZ=0 EndX=117.7 EndY=74.7 EndZ=0
    g5: LineSegment StartX=117.7 StartY=74.7 StartZ=0 EndX=117.7 EndY=-30.7 EndZ=0
    g6: LineSegment StartX=117.7 StartY=-30.7 StartZ=0 EndX=-17.7 EndY=-30.7 EndZ=0
    g7: LineSegment StartX=-17.7 StartY=-30.7 StartZ=0 EndX=-17.7 EndY=74.7 EndZ=0
    g8: LineSegment StartX=-20 StartY=77 StartZ=0 EndX=-17.7 EndY=77 EndZ=0
    g9: LineSegment StartX=-17.7 StartY=77 StartZ=0 EndX=-17.7 EndY=74.7 EndZ=0
    g10: LineSegment StartX=-17.7 StartY=74.7 StartZ=0 EndX=-20 EndY=74.7 EndZ=0
    g11: LineSegment StartX=-20 StartY=74.7 StartZ=0 EndX=-20 EndY=77 EndZ=0
    g12: LineSegment StartX=120 StartY=-33 StartZ=0 EndX=117.7 EndY=-33 EndZ=0
    g13: LineSegment StartX=117.7 StartY=-33 StartZ=0 EndX=117.7 EndY=-30.7 EndZ=0
    g14: LineSegment StartX=117.7 StartY=-30.7 StartZ=0 EndX=120 EndY=-30.7 EndZ=0
    g15: LineSegment StartX=120 StartY=-30.7 StartZ=0 EndX=120 EndY=-33 EndZ=0
  constraints (42):
    c: Coincident(g0,g1)
    c: Coincident(g1,g2)
    c: Coincident(g2,g3)
    c: Coincident(g3,g0)
    c: Horizontal(g0)
    c: Horizontal(g2)
    c: Vertical(g1)
    c: Vertical(g3)
    c: Coincident(g0,g-3)
    c: Coincident(g1,g-4)
    c: Coincident(g4,g5)
    c: Coincident(g5,g6)
    c: Coincident(g6,g7)
    c: Coincident(g7,g4)
    c: Horizontal(g4)
    c: Horizontal(g6)
    c: Vertical(g5)
    c: Vertical(g7)
    c: Coincident(g8,g9)
    c: Coincident(g9,g10)
    c: Coincident(g10,g11)
    c: Coincident(g11,g8)
    c: Horizontal(g8)
    c: Horizontal(g10)
    c: Vertical(g9)
    c: Vertical(g11)
    c: Coincident(g8,g0)
    c: Coincident(g9,g4)
    c: Coincident(g12,g13)
    c: Coincident(g13,g14)
    c: Coincident(g14,g15)
    c: Coincident(g15,g12)
    c: Horizontal(g12)
    c: Horizontal(g14)
    c: Vertical(g13)
    c: Vertical(g15)
    c: Coincident(g12,g1)
    c: Coincident(g13,g5)
    c: Equal(g13,g14)
    c: Equal(g13,g9)
    c: Equal(g9,g10)
    c: DistanceX(g10,g10) = 2.3
FEATURE [PartDesign::Pocket] Pocket008  label="зазор с низом"
  BaseFeature = -> Pad006
  Direction = (0,0,1)
  Length = 3
  Length2 = 5
  Profile = -> Sketch016
  ReferenceAxis = -> Sketch016 [N_Axis]
  Reversed = true
  Type = 1
FEATURE [PartDesign::Fillet] Fillet003  label="сглаж внутр"
  Base = -> Pocket008 [Edge189,Edge175,Edge182,Edge263,Edge257,Edge245,Edge272,Edge328,Edge322,Edge340,Edge334,Edge352,Edge350,Edge310,Edge312,Edge294,Edge300,Edge282,Edge288,Edge319,Edge320,Edge331,Edge332,Edge347,Edge348,Edge280,Edge291,Edge292,Edge307,Edge279,Edge308]
  BaseFeature = -> Pocket008
  Radius = 2
  SupportTransform = false
  UseAllEdges = false
FEATURE [PartDesign::Fillet] Fillet004  label="сглаж внутр dc"
  Base = -> Fillet003 [Edge63]
  BaseFeature = -> Fillet003
  Radius = 6
  SupportTransform = false
  UseAllEdges = false
FEATURE [PartDesign::Fillet] Fillet005  label="сглаж внеш dc"
  Base = -> Fillet004 [Edge412]
  BaseFeature = -> Fillet004
  Radius = 8
  SupportTransform = false
  UseAllEdges = false
FEATURE [PartDesign::Fillet] Fillet006  label="сглаж внеш"
  Base = -> Fillet005 [Edge1,Edge3,Edge4,Edge39,Edge53,Edge38,Edge51]
  BaseFeature = -> Fillet005
  Radius = 4
  SupportTransform = false
  UseAllEdges = false
FEATURE [PartDesign::Body] Body  label="up"
  Group = -> [Sketch,Pad,Sketch001,Pocket,Sketch002,Pad001,Sketch003,Pocket001,Sketch004,Pad002,Sketch005,Pocket002,Sketch006,Pocket003,Sketch013,Pad006,Sketch016,Pocket008,Fillet003,Fillet004,Fillet005,Fillet006]
  Origin = -> Origin021
  Placement = pos=(0,0,15) rot=(0,0,1;0rad)
  Tip = -> Fillet006
